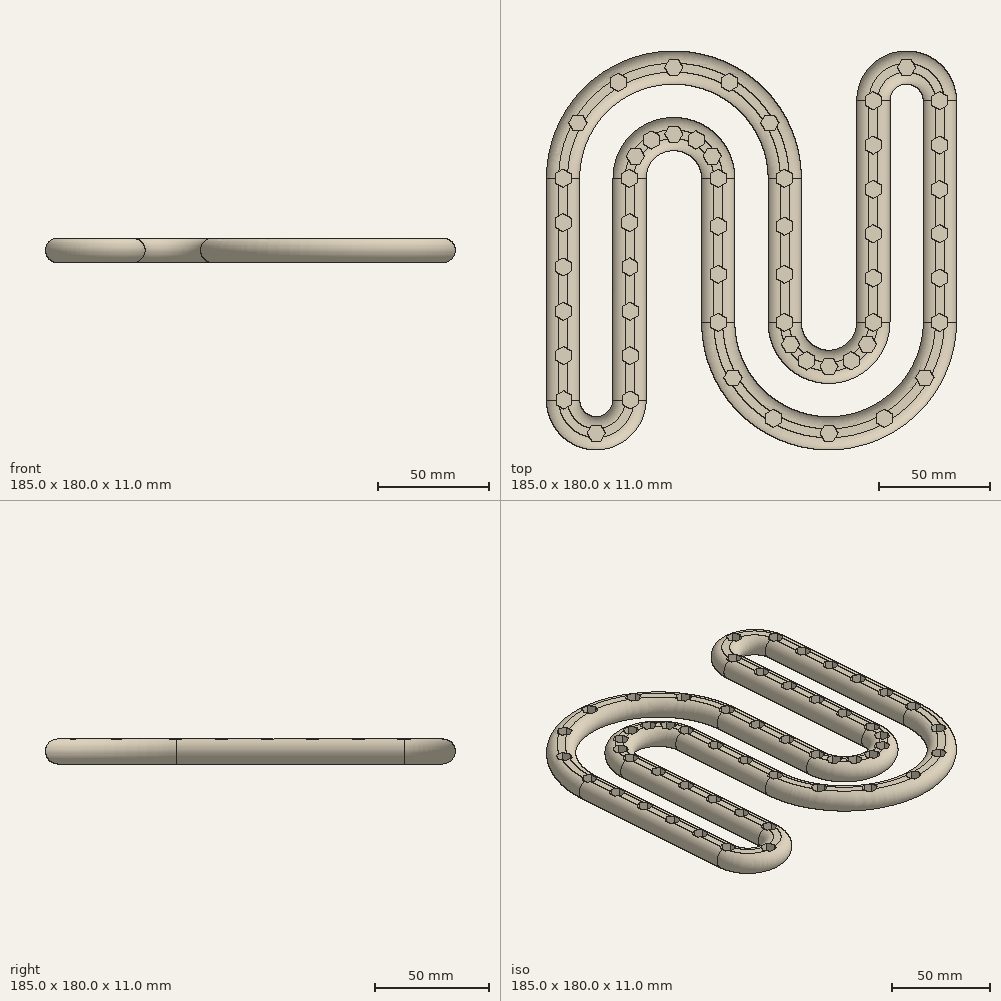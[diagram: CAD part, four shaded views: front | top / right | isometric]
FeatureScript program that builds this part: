
annotation { "Feature Type Name" : "Feature", "Feature Type Description" : "" }
export const myFeature = defineFeature(function(context is Context, id is Id, definition is map)
    precondition{}
    {
        {
            var Q0;
            Q0=qCreatedBy(makeId("Front.planeOp"),FACE);
            var sketch = newSketch(context, id + "F0", { "sketchPlane" : qUnion([Q0])});
            skLineSegment(sketch, "E0.bottom", {"start": v(42.5, 11) * mm, "end": v(57.5, 11) * mm});
            skLineSegment(sketch, "E0.top", {"start": v(42.5, 0) * mm, "end": v(57.5, 0) * mm});
            skLineSegment(sketch, "E0.left", {"start": v(42.5, 11) * mm, "end": v(42.5, 0) * mm});
            skLineSegment(sketch, "E0.right", {"start": v(57.5, 11) * mm, "end": v(57.5, 0) * mm});
            skLineSegment(sketch, "E1", {"start": v(0, 0) * mm, "end": v(0, 22.77) * mm});
            skLineSegment(sketch, "E2.bottom", {"start": v(27.5, 11) * mm, "end": v(12.5, 11) * mm});
            skLineSegment(sketch, "E2.top", {"start": v(27.5, 0) * mm, "end": v(12.5, 0) * mm});
            skLineSegment(sketch, "E2.left", {"start": v(27.5, 11) * mm, "end": v(27.5, 0) * mm});
            skLineSegment(sketch, "E2.right", {"start": v(12.5, 11) * mm, "end": v(12.5, 0) * mm});
            skSolve(sketch);
        }
        {
            var Q0;
            Q0=qSketchRegion(id+"F0",true);
            var Q1;
            Q1=sQuery(id+"F0.wireOp",EDGE,"E1");
            revolve(context, id + "F1", {"entities" : qUnion([Q0]), "axis" : qUnion([Q1]), "revolveType" : RevolveType.ONE_DIRECTION, "angle" : 180 * degree});
        }
        {
            var Q0;
            Q0=makeQuery(id+"F1.opRevolve","CAP_FACE",FACE,{"disambiguationData":[OSD([sQuery(id+"F0.wireOp",EDGE,"E0.bottom"),sQuery(id+"F0.wireOp",EDGE,"E0.top"),sQuery(id+"F0.wireOp",EDGE,"E0.left"),sQuery(id+"F0.wireOp",EDGE,"E0.right")])],"isStart":false});
            var Q1;
            Q1=makeQuery(id+"F1.opRevolve","CAP_FACE",FACE,{"disambiguationData":[OSD([sQuery(id+"F0.wireOp",EDGE,"E2.bottom"),sQuery(id+"F0.wireOp",EDGE,"E2.top"),sQuery(id+"F0.wireOp",EDGE,"E2.left"),sQuery(id+"F0.wireOp",EDGE,"E2.right")])],"isStart":false});
            extrude(context, id + "F2", {"entities" : qUnion([Q0, Q1]), "depth" : 100 * mm});
        }
        {
            var Q0;
            Q0=makeQuery(id+"F1.opRevolve","SWEPT_EDGE",EDGE,{"disambiguationData":[OSD([sQuery(id+"F0.wireOp",EDGE,"E0.bottom"),sQuery(id+"F0.wireOp",EDGE,"E0.left")])]});
            var Q1;
            Q1=makeQuery(id+"F1.opRevolve","SWEPT_EDGE",EDGE,{"disambiguationData":[OSD([sQuery(id+"F0.wireOp",EDGE,"E0.bottom"),sQuery(id+"F0.wireOp",EDGE,"E0.right")])]});
            var Q2;
            Q2=makeQuery(id+"F1.opRevolve","SWEPT_EDGE",EDGE,{"disambiguationData":[OSD([sQuery(id+"F0.wireOp",EDGE,"E0.top"),sQuery(id+"F0.wireOp",EDGE,"E0.right")])]});
            var Q3;
            Q3=makeQuery(id+"F1.opRevolve","SWEPT_EDGE",EDGE,{"disambiguationData":[OSD([sQuery(id+"F0.wireOp",EDGE,"E0.top"),sQuery(id+"F0.wireOp",EDGE,"E0.left")])]});
            fillet(context, id + "F3", {"entities" : qUnion([Q0, Q1, Q2, Q3]), "radius" : 5.5 * mm, "tangentPropagation" : true, "allowEdgeOverflow" : false});
        }
        {
            var Q0;
            Q0=qCreatedBy(makeId("Top.planeOp"),FACE);
            var sketch = newSketch(context, id + "F4", { "sketchPlane" : qUnion([Q0])});
            skCircle(sketch, "E3", {"center": v(0, 0) * mm, "radius": 57.5 * mm});
            skCircle(sketch, "E4", {"center": v(0, 0) * mm, "radius": 42.5 * mm});
            skCircle(sketch, "E5", {"center": v(0, 50) * mm, "radius": 5 * mm});
            skCircle(sketch, "E6", {"center": v(0, 0) * mm, "radius": 50 * mm});
            skCircle(sketch, "E7", {"center": v(21.13, 45.32) * mm, "radius": 7.5 * mm});
            skCircle(sketch, "E8", {"center": v(5.16, 33.28) * mm, "radius": 12.5 * mm});
            skCircle(sketch, "E9", {"center": v(17.95, 49.75) * mm, "radius": 12.96 * mm});
            skLineSegment(sketch, "E10", {"start": v(0, 50) * mm, "end": v(0, 0) * mm});
            skLineSegment(sketch, "E11", {"start": v(21.13, 45.32) * mm, "end": v(0, 0) * mm});
            skSolve(sketch);
        }
        {
            var Q0;
            Q0=makeQuery(id+"F1.opRevolve","SWEPT_EDGE",EDGE,{"disambiguationData":[OSD([sQuery(id+"F0.wireOp",EDGE,"E2.bottom"),sQuery(id+"F0.wireOp",EDGE,"E2.left")])]});
            var Q1;
            Q1=makeQuery(id+"F1.opRevolve","SWEPT_EDGE",EDGE,{"disambiguationData":[OSD([sQuery(id+"F0.wireOp",EDGE,"E2.bottom"),sQuery(id+"F0.wireOp",EDGE,"E2.right")])]});
            var Q2;
            Q2=makeQuery(id+"F1.opRevolve","SWEPT_EDGE",EDGE,{"disambiguationData":[OSD([sQuery(id+"F0.wireOp",EDGE,"E2.top"),sQuery(id+"F0.wireOp",EDGE,"E2.right")])]});
            var Q3;
            Q3=makeQuery(id+"F1.opRevolve","SWEPT_EDGE",EDGE,{"disambiguationData":[OSD([sQuery(id+"F0.wireOp",EDGE,"E2.top"),sQuery(id+"F0.wireOp",EDGE,"E2.left")])]});
            fillet(context, id + "F5", {"entities" : qUnion([Q0, Q1, Q2, Q3]), "radius" : 5.5 * mm, "allowEdgeOverflow" : false});
        }
        {
            var Q0;
            Q0=qCreatedBy(makeId("Top.planeOp"),FACE);
            var sketch = newSketch(context, id + "F6", { "sketchPlane" : qUnion([Q0])});
            skLineSegment(sketch, "E12", {"start": v(0, 0) * mm, "end": v(0, -65) * mm});
            skLineSegment(sketch, "E13", {"start": v(0, -65) * mm, "end": v(70, -65) * mm});
            skSolve(sketch);
        }
        {
            var Q0;
            Q0=qCreatedBy(makeId("Front.planeOp"),FACE);
            cPlane(context, id + "F7", {"entities" : qUnion([Q0]), "cplaneType" : CPlaneType.OFFSET, "offset" : 65 * mm, "width" : 150 * mm, "height" : 150 * mm});
        }
        {
            var Q0;
            Q0=qCreatedBy(id+"F7.planeOp",FACE);
            var sketch = newSketch(context, id + "F8", { "sketchPlane" : qUnion([Q0])});
            skLineSegment(sketch, "E14.bottom", {"start": v(12.5, 0) * mm, "end": v(27.5, 0) * mm});
            skLineSegment(sketch, "E14.top", {"start": v(12.5, 11) * mm, "end": v(27.5, 11) * mm});
            skLineSegment(sketch, "E14.left", {"start": v(12.5, 0) * mm, "end": v(12.5, 11) * mm});
            skLineSegment(sketch, "E14.right", {"start": v(27.5, 0) * mm, "end": v(27.5, 11) * mm});
            skLineSegment(sketch, "E15.bottom", {"start": v(42.5, 0) * mm, "end": v(57.5, 0) * mm});
            skLineSegment(sketch, "E15.top", {"start": v(42.5, 11) * mm, "end": v(57.5, 11) * mm});
            skLineSegment(sketch, "E15.left", {"start": v(42.5, 0) * mm, "end": v(42.5, 11) * mm});
            skLineSegment(sketch, "E15.right", {"start": v(57.5, 0) * mm, "end": v(57.5, 11) * mm});
            skLineSegment(sketch, "E16", {"start": v(0, 0) * mm, "end": v(70, 0) * mm});
            skPoint(sketch, "E16.endSnap0", {"position": v(50, 0) * mm});
            skLineSegment(sketch, "E17", {"start": v(70, 0) * mm, "end": v(70, 23.75) * mm});
            skSolve(sketch);
        }
        {
            var Q0;
            Q0=makeQuery(id+"F8.imprint","IMPRINT",FACE,{"disambiguationData":[TD([[makeQuery(id+"F8.imprint","IMPRINT",EDGE,{"derivedFrom":sQuery(id+"F8.wireOp",EDGE,"E15.top")}),-1.0]])]});
            var Q1;
            Q1=makeQuery(id+"F8.imprint","IMPRINT",FACE,{"disambiguationData":[TD([[makeQuery(id+"F8.imprint","IMPRINT",EDGE,{"derivedFrom":sQuery(id+"F8.wireOp",EDGE,"E14.top")}),-1.0]])]});
            var Q2;
            Q2=sQuery(id+"F8.wireOp",EDGE,"E17");
            revolve(context, id + "F9", {"entities" : qUnion([Q0, Q1]), "axis" : qUnion([Q2]), "revolveType" : RevolveType.ONE_DIRECTION, "angle" : 180 * degree});
        }
        {
            var Q0;
            Q0=makeQuery(id+"F9.opRevolve","SWEPT_EDGE",EDGE,{"disambiguationData":[OSD([sQuery(id+"F8.wireOp",EDGE,"E15.top"),sQuery(id+"F8.wireOp",EDGE,"E15.left")])]});
            var Q1;
            Q1=makeQuery(id+"F9.opRevolve","SWEPT_EDGE",EDGE,{"disambiguationData":[OSD([sQuery(id+"F8.wireOp",EDGE,"E15.top"),sQuery(id+"F8.wireOp",EDGE,"E15.right")])]});
            var Q2;
            Q2=makeQuery(id+"F9.opRevolve","SWEPT_EDGE",EDGE,{"disambiguationData":[OSD([sQuery(id+"F8.wireOp",EDGE,"E15.left"),sQuery(id+"F8.wireOp",EDGE,"E16")])]});
            var Q3;
            Q3=makeQuery(id+"F9.opRevolve","SWEPT_EDGE",EDGE,{"disambiguationData":[OSD([sQuery(id+"F8.wireOp",EDGE,"E15.right"),sQuery(id+"F8.wireOp",EDGE,"E16")])]});
            var Q4;
            Q4=makeQuery(id+"F9.opRevolve","SWEPT_EDGE",EDGE,{"disambiguationData":[OSD([sQuery(id+"F8.wireOp",EDGE,"E14.right"),sQuery(id+"F8.wireOp",EDGE,"E16")])]});
            var Q5;
            Q5=makeQuery(id+"F9.opRevolve","SWEPT_EDGE",EDGE,{"disambiguationData":[OSD([sQuery(id+"F8.wireOp",EDGE,"E14.top"),sQuery(id+"F8.wireOp",EDGE,"E14.right")])]});
            var Q6;
            Q6=makeQuery(id+"F9.opRevolve","SWEPT_EDGE",EDGE,{"disambiguationData":[OSD([sQuery(id+"F8.wireOp",EDGE,"E14.top"),sQuery(id+"F8.wireOp",EDGE,"E14.left")])]});
            var Q7;
            Q7=makeQuery(id+"F9.opRevolve","SWEPT_EDGE",EDGE,{"disambiguationData":[OSD([sQuery(id+"F8.wireOp",EDGE,"E14.left"),sQuery(id+"F8.wireOp",EDGE,"E16")])]});
            fillet(context, id + "F10", {"entities" : qUnion([Q0, Q1, Q2, Q3, Q4, Q5, Q6, Q7]), "radius" : 5.5 * mm, "allowEdgeOverflow" : false});
        }
        {
            var Q0;
            Q0=makeQuery(id+"F9.opRevolve","CAP_FACE",FACE,{"disambiguationData":[OSD([sQuery(id+"F8.wireOp",EDGE,"E14.top"),sQuery(id+"F8.wireOp",EDGE,"E14.left"),sQuery(id+"F8.wireOp",EDGE,"E14.right"),sQuery(id+"F8.wireOp",EDGE,"E16")])],"isStart":false});
            var Q1;
            Q1=makeQuery(id+"F9.opRevolve","CAP_FACE",FACE,{"disambiguationData":[OSD([sQuery(id+"F8.wireOp",EDGE,"E15.top"),sQuery(id+"F8.wireOp",EDGE,"E15.left"),sQuery(id+"F8.wireOp",EDGE,"E15.right"),sQuery(id+"F8.wireOp",EDGE,"E16")])],"isStart":false});
            var Q2;
            Q2=makeQuery(id+"F9.opRevolve","CAP_FACE",FACE,{"disambiguationData":[OSD([sQuery(id+"F8.wireOp",EDGE,"E15.top"),sQuery(id+"F8.wireOp",EDGE,"E15.left"),sQuery(id+"F8.wireOp",EDGE,"E15.right"),sQuery(id+"F8.wireOp",EDGE,"E16")])],"isStart":true});
            var Q3;
            Q3=makeQuery(id+"F9.opRevolve","CAP_FACE",FACE,{"disambiguationData":[OSD([sQuery(id+"F8.wireOp",EDGE,"E14.top"),sQuery(id+"F8.wireOp",EDGE,"E14.left"),sQuery(id+"F8.wireOp",EDGE,"E14.right"),sQuery(id+"F8.wireOp",EDGE,"E16")])],"isStart":true});
            extrude(context, id + "F11", {"entities" : qUnion([Q0, Q1, Q2, Q3]), "depth" : 65 * mm});
        }
        {
            var Q0;
            Q0=makeQuery(id+"F2.opExtrude","SWEPT_EDGE",EDGE,{"disambiguationData":[OSD([sQuery(id+"F0.wireOp",EDGE,"E0.bottom"),sQuery(id+"F0.wireOp",EDGE,"E0.right")])]});
            var Q1;
            Q1=makeQuery(id+"F2.opExtrude","SWEPT_EDGE",EDGE,{"disambiguationData":[OSD([sQuery(id+"F0.wireOp",EDGE,"E0.top"),sQuery(id+"F0.wireOp",EDGE,"E0.right")])]});
            var Q2;
            Q2=makeQuery(id+"F2.opExtrude","SWEPT_EDGE",EDGE,{"disambiguationData":[OSD([sQuery(id+"F0.wireOp",EDGE,"E0.bottom"),sQuery(id+"F0.wireOp",EDGE,"E0.left")])]});
            var Q3;
            Q3=makeQuery(id+"F2.opExtrude","SWEPT_EDGE",EDGE,{"disambiguationData":[OSD([sQuery(id+"F0.wireOp",EDGE,"E0.top"),sQuery(id+"F0.wireOp",EDGE,"E0.left")])]});
            var Q4;
            Q4=makeQuery(id+"F2.opExtrude","SWEPT_EDGE",EDGE,{"disambiguationData":[OSD([sQuery(id+"F0.wireOp",EDGE,"E2.bottom"),sQuery(id+"F0.wireOp",EDGE,"E2.left")])]});
            var Q5;
            Q5=makeQuery(id+"F2.opExtrude","SWEPT_EDGE",EDGE,{"disambiguationData":[OSD([sQuery(id+"F0.wireOp",EDGE,"E2.bottom"),sQuery(id+"F0.wireOp",EDGE,"E2.right")])]});
            var Q6;
            Q6=makeQuery(id+"F2.opExtrude","SWEPT_EDGE",EDGE,{"disambiguationData":[OSD([sQuery(id+"F0.wireOp",EDGE,"E2.top"),sQuery(id+"F0.wireOp",EDGE,"E2.right")])]});
            var Q7;
            Q7=makeQuery(id+"F2.opExtrude","SWEPT_EDGE",EDGE,{"disambiguationData":[OSD([sQuery(id+"F0.wireOp",EDGE,"E2.top"),sQuery(id+"F0.wireOp",EDGE,"E2.left")])]});
            fillet(context, id + "F12", {"entities" : qUnion([Q0, Q1, Q2, Q3, Q4, Q5, Q6, Q7]), "radius" : 5.5 * mm, "allowEdgeOverflow" : false});
        }
        {
            var Q0;
            Q0=makeQuery(id+"F2.opExtrude","CAP_FACE",FACE,{"disambiguationData":[OSD([sQuery(id+"F0.wireOp",EDGE,"E2.bottom"),sQuery(id+"F0.wireOp",EDGE,"E2.top"),sQuery(id+"F0.wireOp",EDGE,"E2.left"),sQuery(id+"F0.wireOp",EDGE,"E2.right")])],"isStart":false});
            var sketch = newSketch(context, id + "F13", { "sketchPlane" : qUnion([Q0])});
            skLineSegment(sketch, "E18", {"start": v(-35, 0) * mm, "end": v(-35, 19.2) * mm});
            skSolve(sketch);
        }
        {
            var Q0;
            {var subQ3=sQuery(id+"F0.wireOp",EDGE,"E2.bottom");Q0=makeQuery(id+"F13.imprint","IMPRINT",FACE,{"disambiguationData":[TD([[makeQuery(id+"F13.imprint","IMPRINT",EDGE,{"derivedFrom":makeQuery(id+"F2.opExtrude","CAP_EDGE",EDGE,{"disambiguationData":[OSD([subQ3])],"isStart":false})}),-1.0]])]});}
            var Q1;
            Q1=sQuery(id+"F13.wireOp",EDGE,"E18");
            revolve(context, id + "F14", {"entities" : qUnion([Q0]), "axis" : qUnion([Q1]), "revolveType" : RevolveType.ONE_DIRECTION, "oppositeDirection" : true, "angle" : 180 * degree});
        }
        {
            var Q0;
            {var subQ0=sQuery(id+"F8.wireOp",EDGE,"E16");var subQ1=sQuery(id+"F8.wireOp",EDGE,"E15.right");var subQ2=sQuery(id+"F8.wireOp",EDGE,"E15.left");var subQ3=sQuery(id+"F8.wireOp",EDGE,"E15.top");Q0=makeQuery(id+"F11.opExtrude","CAP_FACE",FACE,{"disambiguationData":[OSD([subQ3,subQ2,subQ1,subQ0]),TDD([makeQuery(id+"F9.opRevolve","CAP_FACE",FACE,{"disambiguationData":[OSD([subQ3,subQ2,subQ1,subQ0])],"isStart":false})])],"isStart":false});}
            var Q1;
            {var subQ0=sQuery(id+"F8.wireOp",EDGE,"E16");var subQ1=sQuery(id+"F8.wireOp",EDGE,"E14.right");var subQ2=sQuery(id+"F8.wireOp",EDGE,"E14.left");var subQ3=sQuery(id+"F8.wireOp",EDGE,"E14.top");Q1=makeQuery(id+"F11.opExtrude","CAP_FACE",FACE,{"disambiguationData":[OSD([subQ3,subQ2,subQ1,subQ0]),TDD([makeQuery(id+"F9.opRevolve","CAP_FACE",FACE,{"disambiguationData":[OSD([subQ3,subQ2,subQ1,subQ0])],"isStart":false})])],"isStart":false});}
            extrude(context, id + "F15", {"entities" : qUnion([Q0, Q1]), "depth" : 35 * mm});
        }
        {
            var Q0;
            Q0=makeQuery(id+"F15.opExtrude","CAP_FACE",FACE,{"disambiguationData":[OSD([sQuery(id+"F8.wireOp",EDGE,"E15.top"),sQuery(id+"F8.wireOp",EDGE,"E15.left"),sQuery(id+"F8.wireOp",EDGE,"E15.right"),sQuery(id+"F8.wireOp",EDGE,"E16")])],"isStart":false});
            var sketch = newSketch(context, id + "F16", { "sketchPlane" : qUnion([Q0])});
            skLineSegment(sketch, "E19", {"start": v(-105, 0) * mm, "end": v(-105, 22.03) * mm});
            skSolve(sketch);
        }
        {
            var Q0;
            {var subQ3=sQuery(id+"F8.wireOp",EDGE,"E15.top");Q0=makeQuery(id+"F16.imprint","IMPRINT",FACE,{"disambiguationData":[TD([[makeQuery(id+"F16.imprint","IMPRINT",EDGE,{"derivedFrom":makeQuery(id+"F15.opExtrude","CAP_EDGE",EDGE,{"disambiguationData":[OSD([subQ3])],"isStart":false})}),-1.0]])]});}
            var Q1;
            Q1=sQuery(id+"F16.wireOp",EDGE,"E19");
            revolve(context, id + "F17", {"entities" : qUnion([Q0]), "axis" : qUnion([Q1]), "revolveType" : RevolveType.ONE_DIRECTION, "oppositeDirection" : true, "angle" : 180 * degree});
        }
        {
            var Q0;
            Q0=makeQuery(id+"F2.opExtrude","SWEPT_BODY",BODY,{"disambiguationData":[OSD([sQuery(id+"F0.wireOp",EDGE,"E0.bottom"),sQuery(id+"F0.wireOp",EDGE,"E0.top"),sQuery(id+"F0.wireOp",EDGE,"E0.left"),sQuery(id+"F0.wireOp",EDGE,"E0.right")])]});
            var Q1;
            Q1=makeQuery(id+"F14.opRevolve","SWEPT_BODY",BODY,{"disambiguationData":[OSD([sQuery(id+"F0.wireOp",EDGE,"E2.bottom"),sQuery(id+"F0.wireOp",EDGE,"E2.top"),sQuery(id+"F0.wireOp",EDGE,"E2.left"),sQuery(id+"F0.wireOp",EDGE,"E2.right")])]});
            var Q2;
            Q2=makeQuery(id+"F2.opExtrude","SWEPT_BODY",BODY,{"disambiguationData":[OSD([sQuery(id+"F0.wireOp",EDGE,"E2.bottom"),sQuery(id+"F0.wireOp",EDGE,"E2.top"),sQuery(id+"F0.wireOp",EDGE,"E2.left"),sQuery(id+"F0.wireOp",EDGE,"E2.right")])]});
            var Q3;
            Q3=makeQuery(id+"F1.opRevolve","SWEPT_BODY",BODY,{"disambiguationData":[OSD([sQuery(id+"F0.wireOp",EDGE,"E2.bottom"),sQuery(id+"F0.wireOp",EDGE,"E2.top"),sQuery(id+"F0.wireOp",EDGE,"E2.left"),sQuery(id+"F0.wireOp",EDGE,"E2.right")])]});
            var Q4;
            {var subQ0=sQuery(id+"F8.wireOp",EDGE,"E16");var subQ1=sQuery(id+"F8.wireOp",EDGE,"E14.right");var subQ2=sQuery(id+"F8.wireOp",EDGE,"E14.left");var subQ3=sQuery(id+"F8.wireOp",EDGE,"E14.top");Q4=makeQuery(id+"F11.opExtrude","SWEPT_BODY",BODY,{"disambiguationData":[OSD([subQ3,subQ2,subQ1,subQ0]),TDD([makeQuery(id+"F9.opRevolve","CAP_FACE",FACE,{"disambiguationData":[OSD([subQ3,subQ2,subQ1,subQ0])],"isStart":true})])]});}
            var Q5;
            Q5=makeQuery(id+"F9.opRevolve","SWEPT_BODY",BODY,{"disambiguationData":[OSD([sQuery(id+"F8.wireOp",EDGE,"E14.top"),sQuery(id+"F8.wireOp",EDGE,"E14.left"),sQuery(id+"F8.wireOp",EDGE,"E14.right"),sQuery(id+"F8.wireOp",EDGE,"E16")])]});
            var Q6;
            {var subQ0=sQuery(id+"F8.wireOp",EDGE,"E16");var subQ1=sQuery(id+"F8.wireOp",EDGE,"E14.right");var subQ2=sQuery(id+"F8.wireOp",EDGE,"E14.left");var subQ3=sQuery(id+"F8.wireOp",EDGE,"E14.top");Q6=makeQuery(id+"F11.opExtrude","SWEPT_BODY",BODY,{"disambiguationData":[OSD([subQ3,subQ2,subQ1,subQ0]),TDD([makeQuery(id+"F9.opRevolve","CAP_FACE",FACE,{"disambiguationData":[OSD([subQ3,subQ2,subQ1,subQ0])],"isStart":false})])]});}
            var Q7;
            Q7=makeQuery(id+"F15.opExtrude","SWEPT_BODY",BODY,{"disambiguationData":[OSD([sQuery(id+"F8.wireOp",EDGE,"E14.top"),sQuery(id+"F8.wireOp",EDGE,"E14.left"),sQuery(id+"F8.wireOp",EDGE,"E14.right"),sQuery(id+"F8.wireOp",EDGE,"E16")])]});
            var Q8;
            Q8=makeQuery(id+"F17.opRevolve","SWEPT_BODY",BODY,{"disambiguationData":[OSD([sQuery(id+"F8.wireOp",EDGE,"E15.top"),sQuery(id+"F8.wireOp",EDGE,"E15.left"),sQuery(id+"F8.wireOp",EDGE,"E15.right"),sQuery(id+"F8.wireOp",EDGE,"E16")])]});
            var Q9;
            Q9=makeQuery(id+"F15.opExtrude","SWEPT_BODY",BODY,{"disambiguationData":[OSD([sQuery(id+"F8.wireOp",EDGE,"E15.top"),sQuery(id+"F8.wireOp",EDGE,"E15.left"),sQuery(id+"F8.wireOp",EDGE,"E15.right"),sQuery(id+"F8.wireOp",EDGE,"E16")])]});
            var Q10;
            {var subQ0=sQuery(id+"F8.wireOp",EDGE,"E16");var subQ1=sQuery(id+"F8.wireOp",EDGE,"E15.right");var subQ2=sQuery(id+"F8.wireOp",EDGE,"E15.left");var subQ3=sQuery(id+"F8.wireOp",EDGE,"E15.top");Q10=makeQuery(id+"F11.opExtrude","SWEPT_BODY",BODY,{"disambiguationData":[OSD([subQ3,subQ2,subQ1,subQ0]),TDD([makeQuery(id+"F9.opRevolve","CAP_FACE",FACE,{"disambiguationData":[OSD([subQ3,subQ2,subQ1,subQ0])],"isStart":false})])]});}
            var Q11;
            Q11=makeQuery(id+"F9.opRevolve","SWEPT_BODY",BODY,{"disambiguationData":[OSD([sQuery(id+"F8.wireOp",EDGE,"E15.top"),sQuery(id+"F8.wireOp",EDGE,"E15.left"),sQuery(id+"F8.wireOp",EDGE,"E15.right"),sQuery(id+"F8.wireOp",EDGE,"E16")])]});
            var Q12;
            {var subQ0=sQuery(id+"F8.wireOp",EDGE,"E16");var subQ1=sQuery(id+"F8.wireOp",EDGE,"E15.right");var subQ2=sQuery(id+"F8.wireOp",EDGE,"E15.left");var subQ3=sQuery(id+"F8.wireOp",EDGE,"E15.top");Q12=makeQuery(id+"F11.opExtrude","SWEPT_BODY",BODY,{"disambiguationData":[OSD([subQ3,subQ2,subQ1,subQ0]),TDD([makeQuery(id+"F9.opRevolve","CAP_FACE",FACE,{"disambiguationData":[OSD([subQ3,subQ2,subQ1,subQ0])],"isStart":true})])]});}
            var Q13;
            Q13=makeQuery(id+"F1.opRevolve","SWEPT_BODY",BODY,{"disambiguationData":[OSD([sQuery(id+"F0.wireOp",EDGE,"E0.bottom"),sQuery(id+"F0.wireOp",EDGE,"E0.top"),sQuery(id+"F0.wireOp",EDGE,"E0.left"),sQuery(id+"F0.wireOp",EDGE,"E0.right")])]});
            booleanBodies(context, id + "F18", {"operationType" : BooleanOperationType.UNION, "tools" : qUnion([Q0, Q1, Q2, Q3, Q4, Q5, Q6, Q7, Q8, Q9, Q10, Q11, Q12, Q13])});
        }
        {
            var Q0;
            {var subQ0=sQuery(id+"F8.wireOp",EDGE,"E15.top");var subQ1=sQuery(id+"F8.wireOp",EDGE,"E14.top");var subQ2=sQuery(id+"F0.wireOp",EDGE,"E2.bottom");var subQ3=sQuery(id+"F0.wireOp",EDGE,"E0.bottom");Q0=makeQuery(id+"F18.opBoolean","MERGE",FACE,{"derivedFrom":[makeQuery(id+"F1.opRevolve","SWEPT_FACE",FACE,{"disambiguationData":[OSD([subQ3])]}),makeQuery(id+"F1.opRevolve","SWEPT_FACE",FACE,{"disambiguationData":[OSD([subQ2])]}),makeQuery(id+"F9.opRevolve","SWEPT_FACE",FACE,{"disambiguationData":[OSD([subQ1])]}),makeQuery(id+"F9.opRevolve","SWEPT_FACE",FACE,{"disambiguationData":[OSD([subQ0])]}),makeQuery(id+"F11.opExtrude","SWEPT_FACE",FACE,{"disambiguationData":[OSD([subQ1]),TDD([makeQuery(id+"F9.opRevolve","CAP_EDGE",EDGE,{"disambiguationData":[OSD([subQ1])],"isStart":true})])]}),makeQuery(id+"F11.opExtrude","SWEPT_FACE",FACE,{"disambiguationData":[OSD([subQ1]),TDD([makeQuery(id+"F9.opRevolve","CAP_EDGE",EDGE,{"disambiguationData":[OSD([subQ1])],"isStart":false})])]}),makeQuery(id+"F11.opExtrude","SWEPT_FACE",FACE,{"disambiguationData":[OSD([subQ0]),TDD([makeQuery(id+"F9.opRevolve","CAP_EDGE",EDGE,{"disambiguationData":[OSD([subQ0])],"isStart":true})])]}),makeQuery(id+"F11.opExtrude","SWEPT_FACE",FACE,{"disambiguationData":[OSD([subQ0]),TDD([makeQuery(id+"F9.opRevolve","CAP_EDGE",EDGE,{"disambiguationData":[OSD([subQ0])],"isStart":false})])]}),makeQuery(id+"F2.opExtrude","SWEPT_FACE",FACE,{"disambiguationData":[OSD([subQ3])]}),makeQuery(id+"F2.opExtrude","SWEPT_FACE",FACE,{"disambiguationData":[OSD([subQ2])]}),makeQuery(id+"F14.opRevolve","SWEPT_FACE",FACE,{"disambiguationData":[OSD([subQ2])]}),makeQuery(id+"F15.opExtrude","SWEPT_FACE",FACE,{"disambiguationData":[OSD([subQ1])]}),makeQuery(id+"F15.opExtrude","SWEPT_FACE",FACE,{"disambiguationData":[OSD([subQ0])]}),makeQuery(id+"F17.opRevolve","SWEPT_FACE",FACE,{"disambiguationData":[OSD([subQ0])]})]});}
            var sketch = newSketch(context, id + "F19", { "sketchPlane" : qUnion([Q0])});
            skLineSegment(sketch, "E20", {"start": v(-22, -100) * mm, "end": v(-18, -100) * mm});
            skLineSegment(sketch, "E21", {"start": v(-52, 0) * mm, "end": v(-48, 0) * mm});
            skLineSegment(sketch, "E22", {"start": v(-22, 0) * mm, "end": v(-18, 0) * mm});
            skLineSegment(sketch, "E23", {"start": v(18, -65) * mm, "end": v(22, -65) * mm});
            skLineSegment(sketch, "E24", {"start": v(48, -65) * mm, "end": v(52, -65) * mm});
            skLineSegment(sketch, "E25", {"start": v(88, 35) * mm, "end": v(92, 35) * mm});
            skCircle(sketch, "E26.cCircle", {"center": v(-50, 0) * mm, "radius": 3.58 * mm, "construction": true});
            skLineSegment(sketch, "E26.0", {"start": v(-46.43, 2.06) * mm, "end": v(-46.43, -2.06) * mm});
            skLineSegment(sketch, "E26.1", {"start": v(-46.42, -2.06) * mm, "end": v(-50, -4.13) * mm});
            skLineSegment(sketch, "E26.2", {"start": v(-50, -4.13) * mm, "end": v(-53.58, -2.06) * mm});
            skLineSegment(sketch, "E26.3", {"start": v(-53.58, -2.06) * mm, "end": v(-53.58, 2.06) * mm});
            skLineSegment(sketch, "E26.4", {"start": v(-53.58, 2.06) * mm, "end": v(-50, 4.13) * mm});
            skLineSegment(sketch, "E26.5", {"start": v(-50, 4.13) * mm, "end": v(-46.43, 2.06) * mm});
            skPoint(sketch, "E26.0.midPoint", {"position": v(-46.43, 0) * mm});
            skLineSegment(sketch, "E27.0.1.0", {"start": v(-51.92, -20) * mm, "end": v(-47.92, -20) * mm});
            skLineSegment(sketch, "E27.0.1.1", {"start": v(-53.5, -17.94) * mm, "end": v(-49.92, -15.87) * mm});
            skLineSegment(sketch, "E27.0.1.2", {"start": v(-46.35, -22.06) * mm, "end": v(-49.92, -24.13) * mm});
            skLineSegment(sketch, "E27.0.1.3", {"start": v(-49.92, -24.13) * mm, "end": v(-53.5, -22.06) * mm});
            skLineSegment(sketch, "E27.0.1.4", {"start": v(-49.92, -15.87) * mm, "end": v(-46.35, -17.94) * mm});
            skPoint(sketch, "E27.0.1.5", {"position": v(-46.35, -20) * mm});
            skCircle(sketch, "E27.0.1.6", {"center": v(-49.92, -20) * mm, "radius": 3.58 * mm, "construction": true});
            skLineSegment(sketch, "E27.0.1.7", {"start": v(-53.5, -22.06) * mm, "end": v(-53.5, -17.94) * mm});
            skLineSegment(sketch, "E27.0.1.8", {"start": v(-46.35, -17.94) * mm, "end": v(-46.35, -22.06) * mm});
            skLineSegment(sketch, "E27.0.2.0", {"start": v(-51.84, -40) * mm, "end": v(-47.84, -40) * mm});
            skLineSegment(sketch, "E27.0.2.1", {"start": v(-53.42, -37.94) * mm, "end": v(-49.84, -35.87) * mm});
            skLineSegment(sketch, "E27.0.2.2", {"start": v(-46.27, -42.06) * mm, "end": v(-49.84, -44.13) * mm});
            skLineSegment(sketch, "E27.0.2.3", {"start": v(-49.84, -44.13) * mm, "end": v(-53.42, -42.06) * mm});
            skLineSegment(sketch, "E27.0.2.4", {"start": v(-49.84, -35.87) * mm, "end": v(-46.27, -37.94) * mm});
            skPoint(sketch, "E27.0.2.5", {"position": v(-46.27, -40) * mm});
            skCircle(sketch, "E27.0.2.6", {"center": v(-49.84, -40) * mm, "radius": 3.58 * mm, "construction": true});
            skLineSegment(sketch, "E27.0.2.7", {"start": v(-53.42, -42.06) * mm, "end": v(-53.42, -37.94) * mm});
            skLineSegment(sketch, "E27.0.2.8", {"start": v(-46.27, -37.94) * mm, "end": v(-46.27, -42.06) * mm});
            skLineSegment(sketch, "E27.0.3.0", {"start": v(-51.76, -60) * mm, "end": v(-47.76, -60) * mm});
            skLineSegment(sketch, "E27.0.3.1", {"start": v(-53.34, -57.94) * mm, "end": v(-49.76, -55.87) * mm});
            skLineSegment(sketch, "E27.0.3.2", {"start": v(-46.19, -62.06) * mm, "end": v(-49.76, -64.13) * mm});
            skLineSegment(sketch, "E27.0.3.3", {"start": v(-49.76, -64.13) * mm, "end": v(-53.34, -62.06) * mm});
            skLineSegment(sketch, "E27.0.3.4", {"start": v(-49.76, -55.87) * mm, "end": v(-46.19, -57.94) * mm});
            skPoint(sketch, "E27.0.3.5", {"position": v(-46.19, -60) * mm});
            skCircle(sketch, "E27.0.3.6", {"center": v(-49.76, -60) * mm, "radius": 3.58 * mm, "construction": true});
            skLineSegment(sketch, "E27.0.3.7", {"start": v(-53.34, -62.06) * mm, "end": v(-53.34, -57.94) * mm});
            skLineSegment(sketch, "E27.0.3.8", {"start": v(-46.19, -57.94) * mm, "end": v(-46.19, -62.06) * mm});
            skLineSegment(sketch, "E27.0.4.0", {"start": v(-51.68, -80) * mm, "end": v(-47.68, -80) * mm});
            skLineSegment(sketch, "E27.0.4.1", {"start": v(-53.26, -77.94) * mm, "end": v(-49.68, -75.87) * mm});
            skLineSegment(sketch, "E27.0.4.2", {"start": v(-46.1, -82.06) * mm, "end": v(-49.68, -84.13) * mm});
            skLineSegment(sketch, "E27.0.4.3", {"start": v(-49.68, -84.13) * mm, "end": v(-53.26, -82.06) * mm});
            skLineSegment(sketch, "E27.0.4.4", {"start": v(-49.68, -75.87) * mm, "end": v(-46.1, -77.94) * mm});
            skPoint(sketch, "E27.0.4.5", {"position": v(-46.1, -80) * mm});
            skCircle(sketch, "E27.0.4.6", {"center": v(-49.68, -80) * mm, "radius": 3.58 * mm, "construction": true});
            skLineSegment(sketch, "E27.0.4.7", {"start": v(-53.26, -82.06) * mm, "end": v(-53.26, -77.94) * mm});
            skLineSegment(sketch, "E27.0.4.8", {"start": v(-46.1, -77.94) * mm, "end": v(-46.1, -82.06) * mm});
            skLineSegment(sketch, "E27.0.5.0", {"start": v(-51.6, -100) * mm, "end": v(-47.6, -100) * mm});
            skLineSegment(sketch, "E27.0.5.1", {"start": v(-53.18, -97.94) * mm, "end": v(-49.6, -95.87) * mm});
            skLineSegment(sketch, "E27.0.5.2", {"start": v(-46.03, -102.06) * mm, "end": v(-49.6, -104.13) * mm});
            skLineSegment(sketch, "E27.0.5.3", {"start": v(-49.6, -104.13) * mm, "end": v(-53.18, -102.06) * mm});
            skLineSegment(sketch, "E27.0.5.4", {"start": v(-49.6, -95.87) * mm, "end": v(-46.03, -97.94) * mm});
            skPoint(sketch, "E27.0.5.5", {"position": v(-46.03, -100) * mm});
            skCircle(sketch, "E27.0.5.6", {"center": v(-49.6, -100) * mm, "radius": 3.58 * mm, "construction": true});
            skLineSegment(sketch, "E27.0.5.7", {"start": v(-53.18, -102.06) * mm, "end": v(-53.18, -97.94) * mm});
            skLineSegment(sketch, "E27.0.5.8", {"start": v(-46.03, -97.94) * mm, "end": v(-46.03, -102.06) * mm});
            skLineSegment(sketch, "E27.1.0.1", {"start": v(-23.58, 2.06) * mm, "end": v(-20, 4.13) * mm});
            skLineSegment(sketch, "E27.1.0.2", {"start": v(-16.42, -2.06) * mm, "end": v(-20, -4.13) * mm});
            skLineSegment(sketch, "E27.1.0.3", {"start": v(-20, -4.13) * mm, "end": v(-23.58, -2.06) * mm});
            skLineSegment(sketch, "E27.1.0.4", {"start": v(-20, 4.13) * mm, "end": v(-16.43, 2.06) * mm});
            skPoint(sketch, "E27.1.0.5", {"position": v(-16.43, 0) * mm});
            skCircle(sketch, "E27.1.0.6", {"center": v(-20, 0) * mm, "radius": 3.58 * mm, "construction": true});
            skLineSegment(sketch, "E27.1.0.7", {"start": v(-23.58, -2.06) * mm, "end": v(-23.58, 2.06) * mm});
            skLineSegment(sketch, "E27.1.0.8", {"start": v(-16.43, 2.06) * mm, "end": v(-16.43, -2.06) * mm});
            skLineSegment(sketch, "E27.1.1.0", {"start": v(-21.92, -20) * mm, "end": v(-17.92, -20) * mm});
            skLineSegment(sketch, "E27.1.1.1", {"start": v(-23.5, -17.94) * mm, "end": v(-19.92, -15.87) * mm});
            skLineSegment(sketch, "E27.1.1.2", {"start": v(-16.35, -22.06) * mm, "end": v(-19.92, -24.13) * mm});
            skLineSegment(sketch, "E27.1.1.3", {"start": v(-19.92, -24.13) * mm, "end": v(-23.5, -22.06) * mm});
            skLineSegment(sketch, "E27.1.1.4", {"start": v(-19.92, -15.87) * mm, "end": v(-16.35, -17.94) * mm});
            skPoint(sketch, "E27.1.1.5", {"position": v(-16.35, -20) * mm});
            skCircle(sketch, "E27.1.1.6", {"center": v(-19.92, -20) * mm, "radius": 3.58 * mm, "construction": true});
            skLineSegment(sketch, "E27.1.1.7", {"start": v(-23.5, -22.06) * mm, "end": v(-23.5, -17.94) * mm});
            skLineSegment(sketch, "E27.1.1.8", {"start": v(-16.35, -17.94) * mm, "end": v(-16.35, -22.06) * mm});
            skLineSegment(sketch, "E27.1.2.0", {"start": v(-21.84, -40) * mm, "end": v(-17.84, -40) * mm});
            skLineSegment(sketch, "E27.1.2.1", {"start": v(-23.42, -37.94) * mm, "end": v(-19.84, -35.87) * mm});
            skLineSegment(sketch, "E27.1.2.2", {"start": v(-16.27, -42.06) * mm, "end": v(-19.84, -44.13) * mm});
            skLineSegment(sketch, "E27.1.2.3", {"start": v(-19.84, -44.13) * mm, "end": v(-23.42, -42.06) * mm});
            skLineSegment(sketch, "E27.1.2.4", {"start": v(-19.84, -35.87) * mm, "end": v(-16.27, -37.94) * mm});
            skPoint(sketch, "E27.1.2.5", {"position": v(-16.27, -40) * mm});
            skCircle(sketch, "E27.1.2.6", {"center": v(-19.84, -40) * mm, "radius": 3.58 * mm, "construction": true});
            skLineSegment(sketch, "E27.1.2.7", {"start": v(-23.42, -42.06) * mm, "end": v(-23.42, -37.94) * mm});
            skLineSegment(sketch, "E27.1.2.8", {"start": v(-16.27, -37.94) * mm, "end": v(-16.27, -42.06) * mm});
            skLineSegment(sketch, "E27.1.3.0", {"start": v(-21.76, -60) * mm, "end": v(-17.76, -60) * mm});
            skLineSegment(sketch, "E27.1.3.1", {"start": v(-23.34, -57.94) * mm, "end": v(-19.76, -55.87) * mm});
            skLineSegment(sketch, "E27.1.3.2", {"start": v(-16.19, -62.06) * mm, "end": v(-19.76, -64.13) * mm});
            skLineSegment(sketch, "E27.1.3.3", {"start": v(-19.76, -64.13) * mm, "end": v(-23.34, -62.06) * mm});
            skLineSegment(sketch, "E27.1.3.4", {"start": v(-19.76, -55.87) * mm, "end": v(-16.19, -57.94) * mm});
            skPoint(sketch, "E27.1.3.5", {"position": v(-16.19, -60) * mm});
            skCircle(sketch, "E27.1.3.6", {"center": v(-19.76, -60) * mm, "radius": 3.58 * mm, "construction": true});
            skLineSegment(sketch, "E27.1.3.7", {"start": v(-23.34, -62.06) * mm, "end": v(-23.34, -57.94) * mm});
            skLineSegment(sketch, "E27.1.3.8", {"start": v(-16.19, -57.94) * mm, "end": v(-16.19, -62.06) * mm});
            skLineSegment(sketch, "E27.1.4.0", {"start": v(-21.68, -80) * mm, "end": v(-17.68, -80) * mm});
            skLineSegment(sketch, "E27.1.4.1", {"start": v(-23.26, -77.94) * mm, "end": v(-19.68, -75.87) * mm});
            skLineSegment(sketch, "E27.1.4.2", {"start": v(-16.1, -82.06) * mm, "end": v(-19.68, -84.13) * mm});
            skLineSegment(sketch, "E27.1.4.3", {"start": v(-19.68, -84.13) * mm, "end": v(-23.26, -82.06) * mm});
            skLineSegment(sketch, "E27.1.4.4", {"start": v(-19.68, -75.87) * mm, "end": v(-16.1, -77.94) * mm});
            skPoint(sketch, "E27.1.4.5", {"position": v(-16.1, -80) * mm});
            skCircle(sketch, "E27.1.4.6", {"center": v(-19.68, -80) * mm, "radius": 3.58 * mm, "construction": true});
            skLineSegment(sketch, "E27.1.4.7", {"start": v(-23.26, -82.06) * mm, "end": v(-23.26, -77.94) * mm});
            skLineSegment(sketch, "E27.1.4.8", {"start": v(-16.1, -77.94) * mm, "end": v(-16.1, -82.06) * mm});
            skLineSegment(sketch, "E27.1.5.0", {"start": v(-21.6, -100) * mm, "end": v(-17.6, -100) * mm});
            skLineSegment(sketch, "E27.1.5.1", {"start": v(-23.18, -97.94) * mm, "end": v(-19.6, -95.87) * mm});
            skLineSegment(sketch, "E27.1.5.2", {"start": v(-16.03, -102.06) * mm, "end": v(-19.6, -104.13) * mm});
            skLineSegment(sketch, "E27.1.5.3", {"start": v(-19.6, -104.13) * mm, "end": v(-23.18, -102.06) * mm});
            skLineSegment(sketch, "E27.1.5.4", {"start": v(-19.6, -95.87) * mm, "end": v(-16.03, -97.94) * mm});
            skPoint(sketch, "E27.1.5.5", {"position": v(-16.03, -100) * mm});
            skCircle(sketch, "E27.1.5.6", {"center": v(-19.6, -100) * mm, "radius": 3.58 * mm, "construction": true});
            skLineSegment(sketch, "E27.1.5.7", {"start": v(-23.18, -102.06) * mm, "end": v(-23.18, -97.94) * mm});
            skLineSegment(sketch, "E27.1.5.8", {"start": v(-16.03, -97.94) * mm, "end": v(-16.03, -102.06) * mm});
            skLineSegment(sketch, "E27.direction1", {"start": v(-53.58, -2.06) * mm, "end": v(-23.58, -2.06) * mm, "construction": true});
            skLineSegment(sketch, "E27.direction2", {"start": v(-53.58, -2.06) * mm, "end": v(-53.5, -22.06) * mm, "construction": true});
            skLineSegment(sketch, "E28", {"start": v(-35, -113) * mm, "end": v(-35, -117) * mm});
            skCircle(sketch, "E29.cCircle", {"center": v(-35, -115) * mm, "radius": 3.58 * mm, "construction": true});
            skLineSegment(sketch, "E29.0", {"start": v(-32.94, -118.58) * mm, "end": v(-37.06, -118.58) * mm});
            skLineSegment(sketch, "E29.1", {"start": v(-37.06, -118.58) * mm, "end": v(-39.13, -115) * mm});
            skLineSegment(sketch, "E29.2", {"start": v(-39.13, -115) * mm, "end": v(-37.06, -111.43) * mm});
            skLineSegment(sketch, "E29.3", {"start": v(-37.06, -111.43) * mm, "end": v(-32.94, -111.43) * mm});
            skLineSegment(sketch, "E29.4", {"start": v(-32.94, -111.42) * mm, "end": v(-30.87, -115) * mm});
            skLineSegment(sketch, "E29.5", {"start": v(-30.87, -115) * mm, "end": v(-32.94, -118.58) * mm});
            skPoint(sketch, "E29.0.midPoint", {"position": v(-35, -118.58) * mm});
            skPoint(sketch, "E30.1.0", {"position": v(-14.22, 8.21) * mm});
            skPoint(sketch, "E30.1.1", {"position": v(-40.2, 23.21) * mm});
            skCircle(sketch, "E30.1.2", {"center": v(-17.32, 10) * mm, "radius": 3.58 * mm, "construction": true});
            skCircle(sketch, "E30.1.3", {"center": v(-43.3, 25) * mm, "radius": 3.58 * mm, "construction": true});
            skLineSegment(sketch, "E30.1.4", {"start": v(-15.26, 6.42) * mm, "end": v(-19.38, 6.42) * mm});
            skLineSegment(sketch, "E30.1.5", {"start": v(-41.24, 28.57) * mm, "end": v(-39.17, 25) * mm});
            skLineSegment(sketch, "E30.1.6", {"start": v(-19.38, 13.58) * mm, "end": v(-15.26, 13.58) * mm});
            skLineSegment(sketch, "E30.1.7", {"start": v(-15.26, 13.57) * mm, "end": v(-13.2, 10) * mm});
            skLineSegment(sketch, "E30.1.8", {"start": v(-41.24, 21.42) * mm, "end": v(-45.37, 21.42) * mm});
            skLineSegment(sketch, "E30.1.9", {"start": v(-39.17, 25) * mm, "end": v(-41.24, 21.43) * mm});
            skLineSegment(sketch, "E30.1.10", {"start": v(-45.37, 28.58) * mm, "end": v(-41.24, 28.58) * mm});
            skLineSegment(sketch, "E30.1.11", {"start": v(-19.38, 6.42) * mm, "end": v(-21.45, 10) * mm});
            skLineSegment(sketch, "E30.1.12", {"start": v(-21.45, 10) * mm, "end": v(-19.38, 13.57) * mm});
            skLineSegment(sketch, "E30.1.13", {"start": v(-13.2, 10) * mm, "end": v(-15.26, 6.43) * mm});
            skLineSegment(sketch, "E30.1.14", {"start": v(-19.05, 11) * mm, "end": v(-15.59, 9) * mm});
            skLineSegment(sketch, "E30.1.15", {"start": v(-47.43, 25) * mm, "end": v(-45.37, 28.57) * mm});
            skLineSegment(sketch, "E30.1.16", {"start": v(-45.37, 21.43) * mm, "end": v(-47.43, 25) * mm});
            skLineSegment(sketch, "E30.1.17", {"start": v(-19.05, 11) * mm, "end": v(-15.59, 9) * mm});
            skPoint(sketch, "E30.2.0", {"position": v(-8.21, 14.22) * mm});
            skPoint(sketch, "E30.2.1", {"position": v(-23.21, 40.2) * mm});
            skCircle(sketch, "E30.2.2", {"center": v(-10, 17.32) * mm, "radius": 3.58 * mm, "construction": true});
            skCircle(sketch, "E30.2.3", {"center": v(-25, 43.3) * mm, "radius": 3.58 * mm, "construction": true});
            skLineSegment(sketch, "E30.2.4", {"start": v(-10, 13.2) * mm, "end": v(-13.58, 15.26) * mm});
            skLineSegment(sketch, "E30.2.5", {"start": v(-21.43, 45.37) * mm, "end": v(-21.43, 41.24) * mm});
            skLineSegment(sketch, "E30.2.6", {"start": v(-10, 21.45) * mm, "end": v(-6.42, 19.38) * mm});
            skLineSegment(sketch, "E30.2.7", {"start": v(-6.42, 19.38) * mm, "end": v(-6.42, 15.26) * mm});
            skLineSegment(sketch, "E30.2.8", {"start": v(-25, 39.17) * mm, "end": v(-28.58, 41.24) * mm});
            skLineSegment(sketch, "E30.2.9", {"start": v(-21.43, 41.24) * mm, "end": v(-25, 39.17) * mm});
            skLineSegment(sketch, "E30.2.10", {"start": v(-25, 47.43) * mm, "end": v(-21.42, 45.37) * mm});
            skLineSegment(sketch, "E30.2.11", {"start": v(-13.58, 15.26) * mm, "end": v(-13.58, 19.38) * mm});
            skLineSegment(sketch, "E30.2.12", {"start": v(-13.58, 19.38) * mm, "end": v(-10, 21.45) * mm});
            skLineSegment(sketch, "E30.2.13", {"start": v(-6.42, 15.26) * mm, "end": v(-10, 13.2) * mm});
            skLineSegment(sketch, "E30.2.14", {"start": v(-11, 19.05) * mm, "end": v(-9, 15.59) * mm});
            skLineSegment(sketch, "E30.2.15", {"start": v(-28.58, 45.37) * mm, "end": v(-25, 47.43) * mm});
            skLineSegment(sketch, "E30.2.16", {"start": v(-28.58, 41.24) * mm, "end": v(-28.58, 45.37) * mm});
            skLineSegment(sketch, "E30.2.17", {"start": v(-11, 19.05) * mm, "end": v(-9, 15.59) * mm});
            skPoint(sketch, "E30.3.0", {"position": v(0, 16.43) * mm});
            skPoint(sketch, "E30.3.1", {"position": v(0, 46.43) * mm});
            skCircle(sketch, "E30.3.2", {"center": v(0, 20) * mm, "radius": 3.58 * mm, "construction": true});
            skCircle(sketch, "E30.3.3", {"center": v(0, 50) * mm, "radius": 3.58 * mm, "construction": true});
            skLineSegment(sketch, "E30.3.4", {"start": v(-2.06, 16.42) * mm, "end": v(-4.13, 20) * mm});
            skLineSegment(sketch, "E30.3.5", {"start": v(4.13, 50) * mm, "end": v(2.06, 46.43) * mm});
            skLineSegment(sketch, "E30.3.6", {"start": v(2.06, 23.58) * mm, "end": v(4.13, 20) * mm});
            skLineSegment(sketch, "E30.3.7", {"start": v(4.13, 20) * mm, "end": v(2.06, 16.43) * mm});
            skLineSegment(sketch, "E30.3.8", {"start": v(-2.06, 46.42) * mm, "end": v(-4.13, 50) * mm});
            skLineSegment(sketch, "E30.3.9", {"start": v(2.06, 46.43) * mm, "end": v(-2.06, 46.43) * mm});
            skLineSegment(sketch, "E30.3.10", {"start": v(2.06, 53.58) * mm, "end": v(4.13, 50) * mm});
            skLineSegment(sketch, "E30.3.11", {"start": v(-4.13, 20) * mm, "end": v(-2.06, 23.58) * mm});
            skLineSegment(sketch, "E30.3.12", {"start": v(-2.06, 23.58) * mm, "end": v(2.06, 23.58) * mm});
            skLineSegment(sketch, "E30.3.13", {"start": v(2.06, 16.43) * mm, "end": v(-2.06, 16.43) * mm});
            skLineSegment(sketch, "E30.3.14", {"start": v(0, 22) * mm, "end": v(0, 18) * mm});
            skLineSegment(sketch, "E30.3.15", {"start": v(-2.06, 53.58) * mm, "end": v(2.06, 53.58) * mm});
            skLineSegment(sketch, "E30.3.16", {"start": v(-4.13, 50) * mm, "end": v(-2.06, 53.58) * mm});
            skLineSegment(sketch, "E30.3.17", {"start": v(0, 22) * mm, "end": v(0, 18) * mm});
            skPoint(sketch, "E30.4.0", {"position": v(8.21, 14.22) * mm});
            skPoint(sketch, "E30.4.1", {"position": v(23.21, 40.2) * mm});
            skCircle(sketch, "E30.4.2", {"center": v(10, 17.32) * mm, "radius": 3.58 * mm, "construction": true});
            skCircle(sketch, "E30.4.3", {"center": v(25, 43.3) * mm, "radius": 3.58 * mm, "construction": true});
            skLineSegment(sketch, "E30.4.4", {"start": v(6.42, 15.26) * mm, "end": v(6.42, 19.38) * mm});
            skLineSegment(sketch, "E30.4.5", {"start": v(28.57, 41.24) * mm, "end": v(25, 39.17) * mm});
            skLineSegment(sketch, "E30.4.6", {"start": v(13.58, 19.38) * mm, "end": v(13.58, 15.26) * mm});
            skLineSegment(sketch, "E30.4.7", {"start": v(13.57, 15.26) * mm, "end": v(10, 13.2) * mm});
            skLineSegment(sketch, "E30.4.8", {"start": v(21.42, 41.24) * mm, "end": v(21.42, 45.37) * mm});
            skLineSegment(sketch, "E30.4.9", {"start": v(25, 39.17) * mm, "end": v(21.42, 41.24) * mm});
            skLineSegment(sketch, "E30.4.10", {"start": v(28.57, 45.37) * mm, "end": v(28.57, 41.24) * mm});
            skLineSegment(sketch, "E30.4.11", {"start": v(6.42, 19.38) * mm, "end": v(10, 21.45) * mm});
            skLineSegment(sketch, "E30.4.12", {"start": v(10, 21.45) * mm, "end": v(13.57, 19.38) * mm});
            skLineSegment(sketch, "E30.4.13", {"start": v(10, 13.2) * mm, "end": v(6.42, 15.26) * mm});
            skLineSegment(sketch, "E30.4.14", {"start": v(11, 19.05) * mm, "end": v(9, 15.59) * mm});
            skLineSegment(sketch, "E30.4.15", {"start": v(25, 47.43) * mm, "end": v(28.57, 45.37) * mm});
            skLineSegment(sketch, "E30.4.16", {"start": v(21.42, 45.37) * mm, "end": v(25, 47.43) * mm});
            skLineSegment(sketch, "E30.4.17", {"start": v(11, 19.05) * mm, "end": v(9, 15.59) * mm});
            skPoint(sketch, "E30.5.0", {"position": v(14.22, 8.21) * mm});
            skPoint(sketch, "E30.5.1", {"position": v(40.2, 23.21) * mm});
            skCircle(sketch, "E30.5.2", {"center": v(17.32, 10) * mm, "radius": 3.58 * mm, "construction": true});
            skCircle(sketch, "E30.5.3", {"center": v(43.3, 25) * mm, "radius": 3.58 * mm, "construction": true});
            skLineSegment(sketch, "E30.5.4", {"start": v(13.2, 10) * mm, "end": v(15.26, 13.58) * mm});
            skLineSegment(sketch, "E30.5.5", {"start": v(45.37, 21.42) * mm, "end": v(41.24, 21.42) * mm});
            skLineSegment(sketch, "E30.5.6", {"start": v(21.45, 10) * mm, "end": v(19.38, 6.42) * mm});
            skLineSegment(sketch, "E30.5.7", {"start": v(19.38, 6.42) * mm, "end": v(15.26, 6.42) * mm});
            skLineSegment(sketch, "E30.5.8", {"start": v(39.17, 25) * mm, "end": v(41.24, 28.58) * mm});
            skLineSegment(sketch, "E30.5.9", {"start": v(41.24, 21.42) * mm, "end": v(39.17, 25) * mm});
            skLineSegment(sketch, "E30.5.10", {"start": v(47.43, 25) * mm, "end": v(45.37, 21.42) * mm});
            skLineSegment(sketch, "E30.5.11", {"start": v(15.26, 13.58) * mm, "end": v(19.38, 13.58) * mm});
            skLineSegment(sketch, "E30.5.12", {"start": v(19.38, 13.57) * mm, "end": v(21.45, 10) * mm});
            skLineSegment(sketch, "E30.5.13", {"start": v(15.26, 6.42) * mm, "end": v(13.2, 10) * mm});
            skLineSegment(sketch, "E30.5.14", {"start": v(19.05, 11) * mm, "end": v(15.59, 9) * mm});
            skLineSegment(sketch, "E30.5.15", {"start": v(45.37, 28.57) * mm, "end": v(47.43, 25) * mm});
            skLineSegment(sketch, "E30.5.16", {"start": v(41.24, 28.57) * mm, "end": v(45.37, 28.57) * mm});
            skLineSegment(sketch, "E30.5.17", {"start": v(19.05, 11) * mm, "end": v(15.59, 9) * mm});
            skPoint(sketch, "E30.6.0", {"position": v(16.43, 0) * mm});
            skPoint(sketch, "E30.6.1", {"position": v(46.43, 0) * mm});
            skCircle(sketch, "E30.6.2", {"center": v(20, 0) * mm, "radius": 3.58 * mm, "construction": true});
            skCircle(sketch, "E30.6.3", {"center": v(50, 0) * mm, "radius": 3.58 * mm, "construction": true});
            skLineSegment(sketch, "E30.6.4", {"start": v(16.42, 2.06) * mm, "end": v(20, 4.13) * mm});
            skLineSegment(sketch, "E30.6.5", {"start": v(50, -4.13) * mm, "end": v(46.43, -2.06) * mm});
            skLineSegment(sketch, "E30.6.6", {"start": v(23.58, -2.06) * mm, "end": v(20, -4.13) * mm});
            skLineSegment(sketch, "E30.6.7", {"start": v(20, -4.13) * mm, "end": v(16.43, -2.06) * mm});
            skLineSegment(sketch, "E30.6.8", {"start": v(46.42, 2.06) * mm, "end": v(50, 4.13) * mm});
            skLineSegment(sketch, "E30.6.9", {"start": v(46.43, -2.06) * mm, "end": v(46.43, 2.06) * mm});
            skLineSegment(sketch, "E30.6.10", {"start": v(53.58, -2.06) * mm, "end": v(50, -4.13) * mm});
            skLineSegment(sketch, "E30.6.11", {"start": v(20, 4.13) * mm, "end": v(23.58, 2.06) * mm});
            skLineSegment(sketch, "E30.6.12", {"start": v(23.58, 2.06) * mm, "end": v(23.58, -2.06) * mm});
            skLineSegment(sketch, "E30.6.13", {"start": v(16.43, -2.06) * mm, "end": v(16.43, 2.06) * mm});
            skLineSegment(sketch, "E30.6.14", {"start": v(22, 0) * mm, "end": v(18, 0) * mm});
            skLineSegment(sketch, "E30.6.15", {"start": v(53.58, 2.06) * mm, "end": v(53.58, -2.06) * mm});
            skLineSegment(sketch, "E30.6.16", {"start": v(50, 4.13) * mm, "end": v(53.58, 2.06) * mm});
            skLineSegment(sketch, "E30.6.17", {"start": v(22, 0) * mm, "end": v(18, 0) * mm});
            skPoint(sketch, "E30.center", {"position": v(0, 0) * mm});
            skLineSegment(sketch, "E30.anchor1", {"start": v(0, 0) * mm, "end": v(-50, 0) * mm, "construction": true});
            skLineSegment(sketch, "E30.anchor2", {"start": v(0, 0) * mm, "end": v(50, 0) * mm, "construction": true});
            skLineSegment(sketch, "E31", {"start": v(88, -65) * mm, "end": v(92, -65) * mm});
            skLineSegment(sketch, "E32", {"start": v(118, -65) * mm, "end": v(122, -65) * mm});
            skCircle(sketch, "E33.cCircle", {"center": v(120, -65) * mm, "radius": 3.58 * mm, "construction": true});
            skLineSegment(sketch, "E33.0", {"start": v(123.58, -62.94) * mm, "end": v(123.58, -67.06) * mm});
            skLineSegment(sketch, "E33.1", {"start": v(123.58, -67.06) * mm, "end": v(120, -69.13) * mm});
            skLineSegment(sketch, "E33.2", {"start": v(120, -69.13) * mm, "end": v(116.43, -67.06) * mm});
            skLineSegment(sketch, "E33.3", {"start": v(116.43, -67.06) * mm, "end": v(116.43, -62.94) * mm});
            skLineSegment(sketch, "E33.4", {"start": v(116.43, -62.94) * mm, "end": v(120, -60.87) * mm});
            skLineSegment(sketch, "E33.5", {"start": v(120, -60.87) * mm, "end": v(123.58, -62.94) * mm});
            skPoint(sketch, "E33.0.midPoint", {"position": v(123.58, -65) * mm});
            skCircle(sketch, "E34.cCircle", {"center": v(90, -65) * mm, "radius": 3.58 * mm, "construction": true});
            skLineSegment(sketch, "E34.0", {"start": v(93.58, -62.94) * mm, "end": v(93.58, -67.06) * mm});
            skLineSegment(sketch, "E34.1", {"start": v(93.58, -67.06) * mm, "end": v(90, -69.13) * mm});
            skLineSegment(sketch, "E34.2", {"start": v(90, -69.13) * mm, "end": v(86.43, -67.06) * mm});
            skLineSegment(sketch, "E34.3", {"start": v(86.43, -67.06) * mm, "end": v(86.43, -62.94) * mm});
            skLineSegment(sketch, "E34.4", {"start": v(86.43, -62.94) * mm, "end": v(90, -60.87) * mm});
            skLineSegment(sketch, "E34.5", {"start": v(90, -60.87) * mm, "end": v(93.58, -62.94) * mm});
            skPoint(sketch, "E34.0.midPoint", {"position": v(93.58, -65) * mm});
            skPoint(sketch, "E35.1.0", {"position": v(90.42, -76.79) * mm});
            skPoint(sketch, "E35.1.1", {"position": v(116.4, -91.79) * mm});
            skLineSegment(sketch, "E35.1.2", {"start": v(115.37, -93.58) * mm, "end": v(111.24, -93.58) * mm});
            skCircle(sketch, "E35.1.3", {"center": v(113.3, -90) * mm, "radius": 3.58 * mm, "construction": true});
            skCircle(sketch, "E35.1.4", {"center": v(87.32, -75) * mm, "radius": 3.58 * mm, "construction": true});
            skLineSegment(sketch, "E35.1.5", {"start": v(85.59, -74) * mm, "end": v(89.05, -76) * mm});
            skLineSegment(sketch, "E35.1.6", {"start": v(91.45, -75) * mm, "end": v(89.38, -78.58) * mm});
            skLineSegment(sketch, "E35.1.7", {"start": v(83.2, -75) * mm, "end": v(85.26, -71.43) * mm});
            skLineSegment(sketch, "E35.1.8", {"start": v(117.43, -90) * mm, "end": v(115.37, -93.58) * mm});
            skLineSegment(sketch, "E35.1.9", {"start": v(89.38, -71.43) * mm, "end": v(91.45, -75) * mm});
            skLineSegment(sketch, "E35.1.10", {"start": v(85.26, -71.43) * mm, "end": v(89.38, -71.43) * mm});
            skLineSegment(sketch, "E35.1.11", {"start": v(89.38, -78.58) * mm, "end": v(85.26, -78.58) * mm});
            skLineSegment(sketch, "E35.1.12", {"start": v(109.17, -90) * mm, "end": v(111.24, -86.43) * mm});
            skLineSegment(sketch, "E35.1.13", {"start": v(115.37, -86.42) * mm, "end": v(117.43, -90) * mm});
            skLineSegment(sketch, "E35.1.14", {"start": v(111.24, -93.58) * mm, "end": v(109.17, -90) * mm});
            skLineSegment(sketch, "E35.1.15", {"start": v(111.24, -86.43) * mm, "end": v(115.37, -86.43) * mm});
            skLineSegment(sketch, "E35.1.16", {"start": v(85.26, -78.57) * mm, "end": v(83.2, -75) * mm});
            skLineSegment(sketch, "E35.1.17", {"start": v(111.57, -89) * mm, "end": v(115.03, -91) * mm});
            skPoint(sketch, "E35.2.0", {"position": v(81.79, -85.42) * mm});
            skPoint(sketch, "E35.2.1", {"position": v(96.79, -111.4) * mm});
            skLineSegment(sketch, "E35.2.2", {"start": v(95, -112.43) * mm, "end": v(91.42, -110.37) * mm});
            skCircle(sketch, "E35.2.3", {"center": v(95, -108.3) * mm, "radius": 3.58 * mm, "construction": true});
            skCircle(sketch, "E35.2.4", {"center": v(80, -82.32) * mm, "radius": 3.58 * mm, "construction": true});
            skLineSegment(sketch, "E35.2.5", {"start": v(79, -80.59) * mm, "end": v(81, -84.05) * mm});
            skLineSegment(sketch, "E35.2.6", {"start": v(83.58, -84.38) * mm, "end": v(80, -86.45) * mm});
            skLineSegment(sketch, "E35.2.7", {"start": v(76.43, -80.26) * mm, "end": v(80, -78.2) * mm});
            skLineSegment(sketch, "E35.2.8", {"start": v(98.58, -110.37) * mm, "end": v(95, -112.43) * mm});
            skLineSegment(sketch, "E35.2.9", {"start": v(83.58, -80.26) * mm, "end": v(83.58, -84.38) * mm});
            skLineSegment(sketch, "E35.2.10", {"start": v(80, -78.2) * mm, "end": v(83.58, -80.26) * mm});
            skLineSegment(sketch, "E35.2.11", {"start": v(80, -86.45) * mm, "end": v(76.43, -84.38) * mm});
            skLineSegment(sketch, "E35.2.12", {"start": v(91.43, -106.24) * mm, "end": v(95, -104.17) * mm});
            skLineSegment(sketch, "E35.2.13", {"start": v(98.58, -106.24) * mm, "end": v(98.58, -110.37) * mm});
            skLineSegment(sketch, "E35.2.14", {"start": v(91.42, -110.37) * mm, "end": v(91.43, -106.24) * mm});
            skLineSegment(sketch, "E35.2.15", {"start": v(95, -104.17) * mm, "end": v(98.58, -106.24) * mm});
            skLineSegment(sketch, "E35.2.16", {"start": v(76.43, -84.38) * mm, "end": v(76.43, -80.26) * mm});
            skLineSegment(sketch, "E35.2.17", {"start": v(94, -106.57) * mm, "end": v(96, -110.03) * mm});
            skPoint(sketch, "E35.3.0", {"position": v(70, -88.58) * mm});
            skPoint(sketch, "E35.3.1", {"position": v(70, -118.58) * mm});
            skLineSegment(sketch, "E35.3.2", {"start": v(67.94, -118.58) * mm, "end": v(65.87, -115) * mm});
            skCircle(sketch, "E35.3.3", {"center": v(70, -115) * mm, "radius": 3.58 * mm, "construction": true});
            skCircle(sketch, "E35.3.4", {"center": v(70, -85) * mm, "radius": 3.58 * mm, "construction": true});
            skLineSegment(sketch, "E35.3.5", {"start": v(70, -83) * mm, "end": v(70, -87) * mm});
            skLineSegment(sketch, "E35.3.6", {"start": v(72.06, -88.58) * mm, "end": v(67.94, -88.58) * mm});
            skLineSegment(sketch, "E35.3.7", {"start": v(67.94, -81.43) * mm, "end": v(72.06, -81.43) * mm});
            skLineSegment(sketch, "E35.3.8", {"start": v(72.06, -118.58) * mm, "end": v(67.94, -118.58) * mm});
            skLineSegment(sketch, "E35.3.9", {"start": v(74.13, -85) * mm, "end": v(72.06, -88.58) * mm});
            skLineSegment(sketch, "E35.3.10", {"start": v(72.06, -81.43) * mm, "end": v(74.13, -85) * mm});
            skLineSegment(sketch, "E35.3.11", {"start": v(67.94, -88.58) * mm, "end": v(65.87, -85) * mm});
            skLineSegment(sketch, "E35.3.12", {"start": v(67.94, -111.43) * mm, "end": v(72.06, -111.43) * mm});
            skLineSegment(sketch, "E35.3.13", {"start": v(74.13, -115) * mm, "end": v(72.06, -118.58) * mm});
            skLineSegment(sketch, "E35.3.14", {"start": v(65.87, -115) * mm, "end": v(67.94, -111.43) * mm});
            skLineSegment(sketch, "E35.3.15", {"start": v(72.06, -111.43) * mm, "end": v(74.13, -115) * mm});
            skLineSegment(sketch, "E35.3.16", {"start": v(65.87, -85) * mm, "end": v(67.94, -81.43) * mm});
            skLineSegment(sketch, "E35.3.17", {"start": v(70, -113) * mm, "end": v(70, -117) * mm});
            skPoint(sketch, "E35.4.0", {"position": v(58.21, -85.42) * mm});
            skPoint(sketch, "E35.4.1", {"position": v(43.21, -111.4) * mm});
            skLineSegment(sketch, "E35.4.2", {"start": v(41.43, -110.37) * mm, "end": v(41.42, -106.24) * mm});
            skCircle(sketch, "E35.4.3", {"center": v(45, -108.3) * mm, "radius": 3.58 * mm, "construction": true});
            skCircle(sketch, "E35.4.4", {"center": v(60, -82.32) * mm, "radius": 3.58 * mm, "construction": true});
            skLineSegment(sketch, "E35.4.5", {"start": v(61, -80.59) * mm, "end": v(59, -84.05) * mm});
            skLineSegment(sketch, "E35.4.6", {"start": v(60, -86.45) * mm, "end": v(56.43, -84.38) * mm});
            skLineSegment(sketch, "E35.4.7", {"start": v(60, -78.2) * mm, "end": v(63.57, -80.26) * mm});
            skLineSegment(sketch, "E35.4.8", {"start": v(45, -112.43) * mm, "end": v(41.43, -110.37) * mm});
            skLineSegment(sketch, "E35.4.9", {"start": v(63.57, -84.38) * mm, "end": v(60, -86.45) * mm});
            skLineSegment(sketch, "E35.4.10", {"start": v(63.57, -80.26) * mm, "end": v(63.57, -84.38) * mm});
            skLineSegment(sketch, "E35.4.11", {"start": v(56.43, -84.38) * mm, "end": v(56.43, -80.26) * mm});
            skLineSegment(sketch, "E35.4.12", {"start": v(45, -104.17) * mm, "end": v(48.57, -106.24) * mm});
            skLineSegment(sketch, "E35.4.13", {"start": v(48.58, -110.37) * mm, "end": v(45, -112.43) * mm});
            skLineSegment(sketch, "E35.4.14", {"start": v(41.42, -106.24) * mm, "end": v(45, -104.17) * mm});
            skLineSegment(sketch, "E35.4.15", {"start": v(48.58, -106.24) * mm, "end": v(48.58, -110.37) * mm});
            skLineSegment(sketch, "E35.4.16", {"start": v(56.43, -80.26) * mm, "end": v(60, -78.2) * mm});
            skLineSegment(sketch, "E35.4.17", {"start": v(46, -106.57) * mm, "end": v(44, -110.03) * mm});
            skPoint(sketch, "E35.5.0", {"position": v(49.58, -76.79) * mm});
            skPoint(sketch, "E35.5.1", {"position": v(23.6, -91.79) * mm});
            skLineSegment(sketch, "E35.5.2", {"start": v(22.57, -90) * mm, "end": v(24.63, -86.42) * mm});
            skCircle(sketch, "E35.5.3", {"center": v(26.7, -90) * mm, "radius": 3.58 * mm, "construction": true});
            skCircle(sketch, "E35.5.4", {"center": v(52.68, -75) * mm, "radius": 3.58 * mm, "construction": true});
            skLineSegment(sketch, "E35.5.5", {"start": v(54.41, -74) * mm, "end": v(50.95, -76) * mm});
            skLineSegment(sketch, "E35.5.6", {"start": v(50.62, -78.57) * mm, "end": v(48.55, -75) * mm});
            skLineSegment(sketch, "E35.5.7", {"start": v(54.74, -71.43) * mm, "end": v(56.8, -75) * mm});
            skLineSegment(sketch, "E35.5.8", {"start": v(24.63, -93.58) * mm, "end": v(22.57, -90) * mm});
            skLineSegment(sketch, "E35.5.9", {"start": v(54.74, -78.58) * mm, "end": v(50.62, -78.58) * mm});
            skLineSegment(sketch, "E35.5.10", {"start": v(56.8, -75) * mm, "end": v(54.74, -78.58) * mm});
            skLineSegment(sketch, "E35.5.11", {"start": v(48.55, -75) * mm, "end": v(50.62, -71.43) * mm});
            skLineSegment(sketch, "E35.5.12", {"start": v(28.76, -86.43) * mm, "end": v(30.83, -90) * mm});
            skLineSegment(sketch, "E35.5.13", {"start": v(28.76, -93.58) * mm, "end": v(24.63, -93.58) * mm});
            skLineSegment(sketch, "E35.5.14", {"start": v(24.63, -86.42) * mm, "end": v(28.76, -86.43) * mm});
            skLineSegment(sketch, "E35.5.15", {"start": v(30.83, -90) * mm, "end": v(28.76, -93.58) * mm});
            skLineSegment(sketch, "E35.5.16", {"start": v(50.62, -71.43) * mm, "end": v(54.74, -71.43) * mm});
            skLineSegment(sketch, "E35.5.17", {"start": v(28.43, -89) * mm, "end": v(24.97, -91) * mm});
            skPoint(sketch, "E35.6.0", {"position": v(46.42, -65) * mm});
            skPoint(sketch, "E35.6.1", {"position": v(16.42, -65) * mm});
            skLineSegment(sketch, "E35.6.2", {"start": v(16.42, -62.94) * mm, "end": v(20, -60.87) * mm});
            skCircle(sketch, "E35.6.3", {"center": v(20, -65) * mm, "radius": 3.58 * mm, "construction": true});
            skCircle(sketch, "E35.6.4", {"center": v(50, -65) * mm, "radius": 3.58 * mm, "construction": true});
            skLineSegment(sketch, "E35.6.5", {"start": v(52, -65) * mm, "end": v(48, -65) * mm});
            skLineSegment(sketch, "E35.6.6", {"start": v(46.42, -67.06) * mm, "end": v(46.42, -62.94) * mm});
            skLineSegment(sketch, "E35.6.7", {"start": v(53.57, -62.94) * mm, "end": v(53.57, -67.06) * mm});
            skLineSegment(sketch, "E35.6.8", {"start": v(16.42, -67.06) * mm, "end": v(16.42, -62.94) * mm});
            skLineSegment(sketch, "E35.6.9", {"start": v(50, -69.13) * mm, "end": v(46.42, -67.06) * mm});
            skLineSegment(sketch, "E35.6.10", {"start": v(53.57, -67.06) * mm, "end": v(50, -69.13) * mm});
            skLineSegment(sketch, "E35.6.11", {"start": v(46.43, -62.94) * mm, "end": v(50, -60.87) * mm});
            skLineSegment(sketch, "E35.6.12", {"start": v(23.57, -62.94) * mm, "end": v(23.57, -67.06) * mm});
            skLineSegment(sketch, "E35.6.13", {"start": v(20, -69.13) * mm, "end": v(16.42, -67.06) * mm});
            skLineSegment(sketch, "E35.6.14", {"start": v(20, -60.87) * mm, "end": v(23.57, -62.94) * mm});
            skLineSegment(sketch, "E35.6.15", {"start": v(23.57, -67.06) * mm, "end": v(20, -69.13) * mm});
            skLineSegment(sketch, "E35.6.16", {"start": v(50, -60.87) * mm, "end": v(53.57, -62.94) * mm});
            skLineSegment(sketch, "E35.6.17", {"start": v(22, -65) * mm, "end": v(18, -65) * mm});
            skPoint(sketch, "E35.center", {"position": v(70, -65) * mm});
            skLineSegment(sketch, "E35.anchor1", {"start": v(70, -65) * mm, "end": v(120, -65) * mm, "construction": true});
            skLineSegment(sketch, "E35.anchor2", {"start": v(70, -65) * mm, "end": v(20, -65) * mm, "construction": true});
            skPoint(sketch, "E36.0.1.0", {"position": v(16.42, -43.3) * mm});
            skCircle(sketch, "E36.0.1.1", {"center": v(20, -43.3) * mm, "radius": 3.58 * mm, "construction": true});
            skLineSegment(sketch, "E36.0.1.2", {"start": v(16.42, -45.36) * mm, "end": v(16.42, -41.24) * mm});
            skLineSegment(sketch, "E36.0.1.3", {"start": v(23.57, -41.24) * mm, "end": v(23.57, -45.36) * mm});
            skLineSegment(sketch, "E36.0.1.4", {"start": v(16.43, -41.24) * mm, "end": v(20, -39.17) * mm});
            skLineSegment(sketch, "E36.0.1.5", {"start": v(20, -39.17) * mm, "end": v(23.57, -41.24) * mm});
            skLineSegment(sketch, "E36.0.1.6", {"start": v(20, -47.43) * mm, "end": v(16.42, -45.36) * mm});
            skLineSegment(sketch, "E36.0.1.7", {"start": v(22, -43.3) * mm, "end": v(18, -43.3) * mm});
            skLineSegment(sketch, "E36.0.1.8", {"start": v(23.57, -45.36) * mm, "end": v(20, -47.43) * mm});
            skLineSegment(sketch, "E36.0.1.9", {"start": v(18, -43.3) * mm, "end": v(22, -43.3) * mm});
            skPoint(sketch, "E36.0.2.0", {"position": v(16.42, -21.6) * mm});
            skCircle(sketch, "E36.0.2.1", {"center": v(20, -21.6) * mm, "radius": 3.58 * mm, "construction": true});
            skLineSegment(sketch, "E36.0.2.2", {"start": v(16.42, -23.66) * mm, "end": v(16.42, -19.54) * mm});
            skLineSegment(sketch, "E36.0.2.3", {"start": v(23.57, -19.54) * mm, "end": v(23.57, -23.66) * mm});
            skLineSegment(sketch, "E36.0.2.4", {"start": v(16.43, -19.54) * mm, "end": v(20, -17.47) * mm});
            skLineSegment(sketch, "E36.0.2.5", {"start": v(20, -17.47) * mm, "end": v(23.57, -19.54) * mm});
            skLineSegment(sketch, "E36.0.2.6", {"start": v(20, -25.73) * mm, "end": v(16.42, -23.66) * mm});
            skLineSegment(sketch, "E36.0.2.7", {"start": v(22, -21.6) * mm, "end": v(18, -21.6) * mm});
            skLineSegment(sketch, "E36.0.2.8", {"start": v(23.58, -23.66) * mm, "end": v(20, -25.73) * mm});
            skLineSegment(sketch, "E36.0.2.9", {"start": v(18, -21.6) * mm, "end": v(22, -21.6) * mm});
            skLineSegment(sketch, "E36.direction2", {"start": v(16.42, -67.06) * mm, "end": v(16.42, -45.36) * mm, "construction": true});
            skPoint(sketch, "E37.0.1.0", {"position": v(46.42, -43.3) * mm});
            skLineSegment(sketch, "E37.0.1.1", {"start": v(53.57, -45.36) * mm, "end": v(50, -47.43) * mm});
            skCircle(sketch, "E37.0.1.2", {"center": v(50, -43.3) * mm, "radius": 3.58 * mm, "construction": true});
            skLineSegment(sketch, "E37.0.1.3", {"start": v(50, -47.43) * mm, "end": v(46.42, -45.36) * mm});
            skLineSegment(sketch, "E37.0.1.4", {"start": v(46.43, -41.24) * mm, "end": v(50, -39.17) * mm});
            skLineSegment(sketch, "E37.0.1.5", {"start": v(50, -39.17) * mm, "end": v(53.57, -41.24) * mm});
            skLineSegment(sketch, "E37.0.1.6", {"start": v(53.57, -41.24) * mm, "end": v(53.57, -45.36) * mm});
            skLineSegment(sketch, "E37.0.1.7", {"start": v(46.42, -45.36) * mm, "end": v(46.42, -41.24) * mm});
            skLineSegment(sketch, "E37.0.1.8", {"start": v(52, -43.3) * mm, "end": v(48, -43.3) * mm});
            skLineSegment(sketch, "E37.0.1.9", {"start": v(48, -43.3) * mm, "end": v(52, -43.3) * mm});
            skPoint(sketch, "E37.0.2.0", {"position": v(46.42, -21.6) * mm});
            skLineSegment(sketch, "E37.0.2.1", {"start": v(53.57, -23.66) * mm, "end": v(50, -25.73) * mm});
            skCircle(sketch, "E37.0.2.2", {"center": v(50, -21.6) * mm, "radius": 3.58 * mm, "construction": true});
            skLineSegment(sketch, "E37.0.2.3", {"start": v(50, -25.73) * mm, "end": v(46.42, -23.66) * mm});
            skLineSegment(sketch, "E37.0.2.4", {"start": v(46.43, -19.54) * mm, "end": v(50, -17.47) * mm});
            skLineSegment(sketch, "E37.0.2.5", {"start": v(50, -17.47) * mm, "end": v(53.57, -19.54) * mm});
            skLineSegment(sketch, "E37.0.2.6", {"start": v(53.57, -19.54) * mm, "end": v(53.57, -23.66) * mm});
            skLineSegment(sketch, "E37.0.2.7", {"start": v(46.42, -23.66) * mm, "end": v(46.42, -19.54) * mm});
            skLineSegment(sketch, "E37.0.2.8", {"start": v(52, -21.6) * mm, "end": v(48, -21.6) * mm});
            skLineSegment(sketch, "E37.0.2.9", {"start": v(48, -21.6) * mm, "end": v(52, -21.6) * mm});
            skLineSegment(sketch, "E37.direction2", {"start": v(46.42, -67.06) * mm, "end": v(46.42, -45.36) * mm, "construction": true});
            skPoint(sketch, "E38.0.1.0", {"position": v(123.58, -45) * mm});
            skCircle(sketch, "E38.0.1.1", {"center": v(120, -45) * mm, "radius": 3.58 * mm, "construction": true});
            skLineSegment(sketch, "E38.0.1.2", {"start": v(123.58, -42.94) * mm, "end": v(123.58, -47.06) * mm});
            skLineSegment(sketch, "E38.0.1.3", {"start": v(116.43, -42.94) * mm, "end": v(120, -40.87) * mm});
            skLineSegment(sketch, "E38.0.1.4", {"start": v(123.58, -47.06) * mm, "end": v(120, -49.13) * mm});
            skLineSegment(sketch, "E38.0.1.5", {"start": v(120, -40.87) * mm, "end": v(123.58, -42.94) * mm});
            skLineSegment(sketch, "E38.0.1.6", {"start": v(116.43, -47.06) * mm, "end": v(116.43, -42.94) * mm});
            skLineSegment(sketch, "E38.0.1.7", {"start": v(118, -45) * mm, "end": v(122, -45) * mm});
            skLineSegment(sketch, "E38.0.1.8", {"start": v(120, -49.13) * mm, "end": v(116.43, -47.06) * mm});
            skPoint(sketch, "E38.0.2.0", {"position": v(123.58, -25) * mm});
            skCircle(sketch, "E38.0.2.1", {"center": v(120, -25) * mm, "radius": 3.58 * mm, "construction": true});
            skLineSegment(sketch, "E38.0.2.2", {"start": v(123.58, -22.94) * mm, "end": v(123.58, -27.06) * mm});
            skLineSegment(sketch, "E38.0.2.3", {"start": v(116.43, -22.94) * mm, "end": v(120, -20.87) * mm});
            skLineSegment(sketch, "E38.0.2.4", {"start": v(123.58, -27.06) * mm, "end": v(120, -29.13) * mm});
            skLineSegment(sketch, "E38.0.2.5", {"start": v(120, -20.87) * mm, "end": v(123.58, -22.94) * mm});
            skLineSegment(sketch, "E38.0.2.6", {"start": v(116.43, -27.06) * mm, "end": v(116.43, -22.94) * mm});
            skLineSegment(sketch, "E38.0.2.7", {"start": v(118, -25) * mm, "end": v(122, -25) * mm});
            skLineSegment(sketch, "E38.0.2.8", {"start": v(120, -29.13) * mm, "end": v(116.43, -27.06) * mm});
            skPoint(sketch, "E38.0.3.0", {"position": v(123.58, -5) * mm});
            skCircle(sketch, "E38.0.3.1", {"center": v(120, -5) * mm, "radius": 3.58 * mm, "construction": true});
            skLineSegment(sketch, "E38.0.3.2", {"start": v(123.58, -2.94) * mm, "end": v(123.58, -7.06) * mm});
            skLineSegment(sketch, "E38.0.3.3", {"start": v(116.43, -2.94) * mm, "end": v(120, -0.87) * mm});
            skLineSegment(sketch, "E38.0.3.4", {"start": v(123.58, -7.06) * mm, "end": v(120, -9.13) * mm});
            skLineSegment(sketch, "E38.0.3.5", {"start": v(120, -0.87) * mm, "end": v(123.58, -2.94) * mm});
            skLineSegment(sketch, "E38.0.3.6", {"start": v(116.43, -7.06) * mm, "end": v(116.43, -2.94) * mm});
            skLineSegment(sketch, "E38.0.3.7", {"start": v(118, -5) * mm, "end": v(122, -5) * mm});
            skLineSegment(sketch, "E38.0.3.8", {"start": v(120, -9.13) * mm, "end": v(116.43, -7.06) * mm});
            skPoint(sketch, "E38.0.4.0", {"position": v(123.58, 15) * mm});
            skCircle(sketch, "E38.0.4.1", {"center": v(120, 15) * mm, "radius": 3.58 * mm, "construction": true});
            skLineSegment(sketch, "E38.0.4.2", {"start": v(123.58, 17.06) * mm, "end": v(123.58, 12.94) * mm});
            skLineSegment(sketch, "E38.0.4.3", {"start": v(116.43, 17.06) * mm, "end": v(120, 19.13) * mm});
            skLineSegment(sketch, "E38.0.4.4", {"start": v(123.58, 12.94) * mm, "end": v(120, 10.87) * mm});
            skLineSegment(sketch, "E38.0.4.5", {"start": v(120, 19.13) * mm, "end": v(123.58, 17.06) * mm});
            skLineSegment(sketch, "E38.0.4.6", {"start": v(116.43, 12.94) * mm, "end": v(116.43, 17.06) * mm});
            skLineSegment(sketch, "E38.0.4.7", {"start": v(118, 15) * mm, "end": v(122, 15) * mm});
            skLineSegment(sketch, "E38.0.4.8", {"start": v(120, 10.87) * mm, "end": v(116.43, 12.94) * mm});
            skPoint(sketch, "E38.0.5.0", {"position": v(123.58, 35) * mm});
            skCircle(sketch, "E38.0.5.1", {"center": v(120, 35) * mm, "radius": 3.58 * mm, "construction": true});
            skLineSegment(sketch, "E38.0.5.2", {"start": v(123.58, 37.06) * mm, "end": v(123.58, 32.94) * mm});
            skLineSegment(sketch, "E38.0.5.3", {"start": v(116.43, 37.06) * mm, "end": v(120, 39.13) * mm});
            skLineSegment(sketch, "E38.0.5.4", {"start": v(123.58, 32.94) * mm, "end": v(120, 30.87) * mm});
            skLineSegment(sketch, "E38.0.5.5", {"start": v(120, 39.13) * mm, "end": v(123.58, 37.06) * mm});
            skLineSegment(sketch, "E38.0.5.6", {"start": v(116.43, 32.94) * mm, "end": v(116.43, 37.06) * mm});
            skLineSegment(sketch, "E38.0.5.7", {"start": v(118, 35) * mm, "end": v(122, 35) * mm});
            skLineSegment(sketch, "E38.0.5.8", {"start": v(120, 30.87) * mm, "end": v(116.43, 32.94) * mm});
            skLineSegment(sketch, "E38.direction2", {"start": v(116.43, -67.06) * mm, "end": v(116.43, -47.06) * mm, "construction": true});
            skCircle(sketch, "E39.0.1.0", {"center": v(90, -45) * mm, "radius": 3.58 * mm, "construction": true});
            skLineSegment(sketch, "E39.0.1.1", {"start": v(90, -40.87) * mm, "end": v(93.58, -42.94) * mm});
            skPoint(sketch, "E39.0.1.2", {"position": v(93.58, -45) * mm});
            skLineSegment(sketch, "E39.0.1.3", {"start": v(93.58, -47.06) * mm, "end": v(90, -49.13) * mm});
            skLineSegment(sketch, "E39.0.1.4", {"start": v(86.43, -47.06) * mm, "end": v(86.43, -42.94) * mm});
            skLineSegment(sketch, "E39.0.1.5", {"start": v(90, -49.13) * mm, "end": v(86.43, -47.06) * mm});
            skLineSegment(sketch, "E39.0.1.6", {"start": v(88, -45) * mm, "end": v(92, -45) * mm});
            skLineSegment(sketch, "E39.0.1.7", {"start": v(93.58, -42.94) * mm, "end": v(93.58, -47.06) * mm});
            skLineSegment(sketch, "E39.0.1.8", {"start": v(86.43, -42.94) * mm, "end": v(90, -40.87) * mm});
            skCircle(sketch, "E39.0.2.0", {"center": v(90, -25) * mm, "radius": 3.58 * mm, "construction": true});
            skLineSegment(sketch, "E39.0.2.1", {"start": v(90, -20.87) * mm, "end": v(93.58, -22.94) * mm});
            skPoint(sketch, "E39.0.2.2", {"position": v(93.58, -25) * mm});
            skLineSegment(sketch, "E39.0.2.3", {"start": v(93.58, -27.06) * mm, "end": v(90, -29.13) * mm});
            skLineSegment(sketch, "E39.0.2.4", {"start": v(86.43, -27.06) * mm, "end": v(86.43, -22.94) * mm});
            skLineSegment(sketch, "E39.0.2.5", {"start": v(90, -29.13) * mm, "end": v(86.43, -27.06) * mm});
            skLineSegment(sketch, "E39.0.2.6", {"start": v(88, -25) * mm, "end": v(92, -25) * mm});
            skLineSegment(sketch, "E39.0.2.7", {"start": v(93.58, -22.94) * mm, "end": v(93.58, -27.06) * mm});
            skLineSegment(sketch, "E39.0.2.8", {"start": v(86.43, -22.94) * mm, "end": v(90, -20.87) * mm});
            skCircle(sketch, "E39.0.3.0", {"center": v(90, -5) * mm, "radius": 3.58 * mm, "construction": true});
            skLineSegment(sketch, "E39.0.3.1", {"start": v(90, -0.87) * mm, "end": v(93.58, -2.94) * mm});
            skPoint(sketch, "E39.0.3.2", {"position": v(93.58, -5) * mm});
            skLineSegment(sketch, "E39.0.3.3", {"start": v(93.58, -7.06) * mm, "end": v(90, -9.13) * mm});
            skLineSegment(sketch, "E39.0.3.4", {"start": v(86.43, -7.06) * mm, "end": v(86.43, -2.94) * mm});
            skLineSegment(sketch, "E39.0.3.5", {"start": v(90, -9.13) * mm, "end": v(86.43, -7.06) * mm});
            skLineSegment(sketch, "E39.0.3.6", {"start": v(88, -5) * mm, "end": v(92, -5) * mm});
            skLineSegment(sketch, "E39.0.3.7", {"start": v(93.58, -2.94) * mm, "end": v(93.58, -7.06) * mm});
            skLineSegment(sketch, "E39.0.3.8", {"start": v(86.43, -2.94) * mm, "end": v(90, -0.87) * mm});
            skCircle(sketch, "E39.0.4.0", {"center": v(90, 15) * mm, "radius": 3.58 * mm, "construction": true});
            skLineSegment(sketch, "E39.0.4.1", {"start": v(90, 19.13) * mm, "end": v(93.58, 17.06) * mm});
            skPoint(sketch, "E39.0.4.2", {"position": v(93.58, 15) * mm});
            skLineSegment(sketch, "E39.0.4.3", {"start": v(93.58, 12.94) * mm, "end": v(90, 10.87) * mm});
            skLineSegment(sketch, "E39.0.4.4", {"start": v(86.43, 12.94) * mm, "end": v(86.43, 17.06) * mm});
            skLineSegment(sketch, "E39.0.4.5", {"start": v(90, 10.87) * mm, "end": v(86.43, 12.94) * mm});
            skLineSegment(sketch, "E39.0.4.6", {"start": v(88, 15) * mm, "end": v(92, 15) * mm});
            skLineSegment(sketch, "E39.0.4.7", {"start": v(93.58, 17.06) * mm, "end": v(93.58, 12.94) * mm});
            skLineSegment(sketch, "E39.0.4.8", {"start": v(86.43, 17.06) * mm, "end": v(90, 19.13) * mm});
            skCircle(sketch, "E39.0.5.0", {"center": v(90, 35) * mm, "radius": 3.58 * mm, "construction": true});
            skLineSegment(sketch, "E39.0.5.1", {"start": v(90, 39.13) * mm, "end": v(93.58, 37.06) * mm});
            skPoint(sketch, "E39.0.5.2", {"position": v(93.58, 35) * mm});
            skLineSegment(sketch, "E39.0.5.3", {"start": v(93.58, 32.94) * mm, "end": v(90, 30.87) * mm});
            skLineSegment(sketch, "E39.0.5.4", {"start": v(86.43, 32.94) * mm, "end": v(86.43, 37.06) * mm});
            skLineSegment(sketch, "E39.0.5.5", {"start": v(90, 30.87) * mm, "end": v(86.43, 32.94) * mm});
            skLineSegment(sketch, "E39.0.5.7", {"start": v(93.58, 37.06) * mm, "end": v(93.58, 32.94) * mm});
            skLineSegment(sketch, "E39.0.5.8", {"start": v(86.43, 37.06) * mm, "end": v(90, 39.13) * mm});
            skLineSegment(sketch, "E39.direction1", {"start": v(86.43, -67.06) * mm, "end": v(111.43, -67.06) * mm, "construction": true});
            skLineSegment(sketch, "E39.direction2", {"start": v(86.43, -67.06) * mm, "end": v(86.43, -47.06) * mm, "construction": true});
            skLineSegment(sketch, "E40", {"start": v(105, 48) * mm, "end": v(105, 52) * mm});
            skCircle(sketch, "E41.cCircle", {"center": v(105, 50) * mm, "radius": 3.58 * mm, "construction": true});
            skLineSegment(sketch, "E41.0", {"start": v(102.94, 53.57) * mm, "end": v(107.06, 53.57) * mm});
            skLineSegment(sketch, "E41.1", {"start": v(107.06, 53.57) * mm, "end": v(109.13, 50) * mm});
            skLineSegment(sketch, "E41.2", {"start": v(109.13, 50) * mm, "end": v(107.06, 46.42) * mm});
            skLineSegment(sketch, "E41.3", {"start": v(107.06, 46.42) * mm, "end": v(102.94, 46.42) * mm});
            skLineSegment(sketch, "E41.4", {"start": v(102.94, 46.42) * mm, "end": v(100.87, 50) * mm});
            skLineSegment(sketch, "E41.5", {"start": v(100.87, 50) * mm, "end": v(102.94, 53.57) * mm});
            skPoint(sketch, "E41.0.midPoint", {"position": v(105, 53.57) * mm});
            skSolve(sketch);
        }
        {
            var Q0;
            Q0 = qSketchRegion(id + "F19", true);
            extrude(context, id + "F20", {"entities" : qUnion([Q0]), "operationType" : NewBodyOperationType.REMOVE, "oppositeDirection" : true, "depth" : 8.5 * mm});
        }
    });
